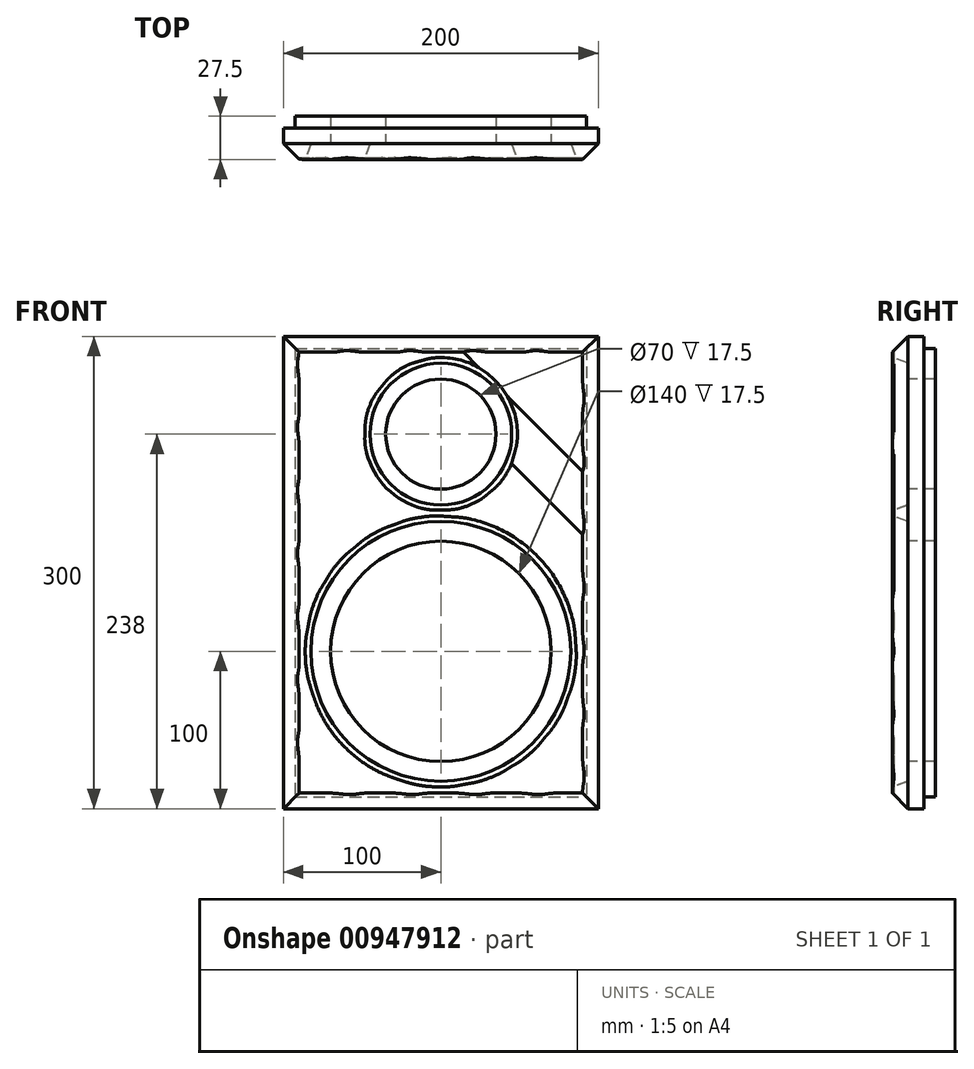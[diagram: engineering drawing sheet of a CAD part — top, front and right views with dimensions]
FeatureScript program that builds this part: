
annotation { "Feature Type Name" : "Feature", "Feature Type Description" : "" }
export const myFeature = defineFeature(function(context is Context, id is Id, definition is map)
    precondition{}
    {
        {
            var Q0;
            Q0=qCreatedBy(makeId("Right.planeOp"),FACE);
            cPlane(context, id + "F0", {"entities" : qUnion([Q0]), "cplaneType" : CPlaneType.OFFSET, "offset" : 100 * mm, "width" : 150 * mm, "height" : 150 * mm});
        }
        {
            var Q0;
            Q0=qCreatedBy(makeId("Right.planeOp"),FACE);
            cPlane(context, id + "F1", {"entities" : qUnion([Q0]), "cplaneType" : CPlaneType.OFFSET, "offset" : 100 * mm, "oppositeDirection" : true, "width" : 150 * mm, "height" : 150 * mm});
        }
        {
            var Q0;
            Q0=qCreatedBy(makeId("Right.planeOp"),FACE);
            cPlane(context, id + "F2", {"entities" : qUnion([Q0]), "cplaneType" : CPlaneType.OFFSET, "offset" : (100 - 7.5) * mm, "width" : 150 * mm, "height" : 150 * mm});
        }
        {
            var Q0;
            Q0=qCreatedBy(makeId("Right.planeOp"),FACE);
            cPlane(context, id + "F3", {"entities" : qUnion([Q0]), "cplaneType" : CPlaneType.OFFSET, "offset" : (100 - 7.5) * mm, "oppositeDirection" : true, "width" : 150 * mm, "height" : 150 * mm});
        }
        {
            var Q0;
            Q0=qCreatedBy(makeId("Top.planeOp"),FACE);
            cPlane(context, id + "F4", {"entities" : qUnion([Q0]), "cplaneType" : CPlaneType.OFFSET, "offset" : 7.7 * mm, "width" : 150 * mm, "height" : 150 * mm});
        }
        {
            var Q0;
            Q0=qCreatedBy(makeId("Top.planeOp"),FACE);
            cPlane(context, id + "F5", {"entities" : qUnion([Q0]), "cplaneType" : CPlaneType.OFFSET, "offset" : 300 * mm, "width" : 150 * mm, "height" : 150 * mm});
        }
        {
            var Q0;
            Q0=qCreatedBy(makeId("Top.planeOp"),FACE);
            cPlane(context, id + "F6", {"entities" : qUnion([Q0]), "cplaneType" : CPlaneType.OFFSET, "offset" : (300 - 7.5) * mm, "width" : 150 * mm, "height" : 150 * mm});
        }
        {
            var Q0;
            Q0=qCreatedBy(makeId("Front.planeOp"),FACE);
            cPlane(context, id + "F7", {"entities" : qUnion([Q0]), "cplaneType" : CPlaneType.OFFSET, "offset" : 150 * mm, "width" : 150 * mm, "height" : 150 * mm});
        }
        {
            var Q0;
            Q0=qCreatedBy(makeId("Front.planeOp"),FACE);
            cPlane(context, id + "F8", {"entities" : qUnion([Q0]), "cplaneType" : CPlaneType.OFFSET, "offset" : (150 - 7.5) * mm, "width" : 150 * mm, "height" : 150 * mm});
        }
        {
            var Q0;
            Q0=qCreatedBy(id+"F8.planeOp",FACE);
            var sketch = newSketch(context, id + "F9", { "sketchPlane" : qUnion([Q0])});
            skLineSegment(sketch, "E0.bottom", {"start": v(-92.5, 292.5) * mm, "end": v(92.5, 292.5) * mm});
            skLineSegment(sketch, "E0.top", {"start": v(-92.5, 7.7) * mm, "end": v(92.5, 7.7) * mm});
            skLineSegment(sketch, "E0.left", {"start": v(-92.5, 292.5) * mm, "end": v(-92.5, 7.7) * mm});
            skLineSegment(sketch, "E0.right", {"start": v(92.5, 292.5) * mm, "end": v(92.5, 7.7) * mm});
            skSolve(sketch);
        }
        {
            var Q0;
            Q0=makeQuery(id+"F9.imprint","IMPRINT",FACE,{"disambiguationData":[TD([[makeQuery(id+"F9.imprint","IMPRINT",EDGE,{"derivedFrom":sQuery(id+"F9.wireOp",EDGE,"E0.bottom")}),-1.0]])]});
            extrude(context, id + "F10", {"entities" : qUnion([Q0]), "depth" : 7.5 * mm, "offsetDistance" : 25 * mm});
        }
        {
            var Q0;
            Q0=qCreatedBy(id+"F7.planeOp",FACE);
            var sketch = newSketch(context, id + "F11", { "sketchPlane" : qUnion([Q0])});
            skLineSegment(sketch, "E1.bottom", {"start": v(-100, 300) * mm, "end": v(100, 300) * mm});
            skLineSegment(sketch, "E1.top", {"start": v(-100, 0) * mm, "end": v(100, 0) * mm});
            skLineSegment(sketch, "E1.left", {"start": v(-100, 300) * mm, "end": v(-100, 0) * mm});
            skLineSegment(sketch, "E1.right", {"start": v(100, 300) * mm, "end": v(100, 0) * mm});
            skSolve(sketch);
        }
        {
            var Q0;
            Q0=makeQuery(id+"F11.imprint","IMPRINT",FACE,{"disambiguationData":[TD([[makeQuery(id+"F11.imprint","IMPRINT",EDGE,{"derivedFrom":sQuery(id+"F11.wireOp",EDGE,"E1.bottom")}),-1.0]])]});
            extrude(context, id + "F12", {"entities" : qUnion([Q0]), "operationType" : NewBodyOperationType.ADD, "depth" : 20 * mm, "offsetDistance" : 25 * mm});
        }
        {
            var Q0;
            Q0=qCreatedBy(id+"F0.planeOp",FACE);
            var sketch = newSketch(context, id + "F13", { "sketchPlane" : qUnion([Q0])});
            skLineSegment(sketch, "E2", {"start": v(-220, 0) * mm, "end": v(-220, 300) * mm});
            skLineSegment(sketch, "E3", {"start": v(-220, 300) * mm, "end": v(-180, 300) * mm});
            skLineSegment(sketch, "E4", {"start": v(-180, 300) * mm, "end": v(-180, 0) * mm});
            skLineSegment(sketch, "E5", {"start": v(-180, 0) * mm, "end": v(-220, 0) * mm});
            skSolve(sketch);
        }
        {
            var Q0;
            Q0=qCreatedBy(makeId("Front.planeOp"),FACE);
            cPlane(context, id + "F14", {"entities" : qUnion([Q0]), "cplaneType" : CPlaneType.OFFSET, "offset" : 300 * mm, "width" : 150 * mm, "height" : 150 * mm});
        }
        {
            var Q0;
            Q0=qCreatedBy(makeId("Front.planeOp"),FACE);
            cPlane(context, id + "F15", {"entities" : qUnion([Q0]), "cplaneType" : CPlaneType.OFFSET, "offset" : 160 * mm, "width" : 150 * mm, "height" : 150 * mm});
        }
        {
            var Q0;
            Q0=qCreatedBy(id+"F14.planeOp",FACE);
            var sketch = newSketch(context, id + "F16", { "sketchPlane" : qUnion([Q0])});
            skCircle(sketch, "E6", {"center": v(0, 100) * mm, "radius": 70 * mm});
            skSolve(sketch);
        }
        {
            var Q0;
            Q0=qSketchRegion(id+"F16",true);
            var Q1;
            Q1=qCreatedBy(id+"F8.planeOp",FACE);
            extrude(context, id + "F17", {"entities" : qUnion([Q0]), "operationType" : NewBodyOperationType.REMOVE, "endBound" : BoundingType.UP_TO_SURFACE, "oppositeDirection" : true, "depth" : 25 * mm, "endBoundEntityFace" : qUnion([Q1]), "offsetDistance" : 25 * mm});
        }
        {
            var Q0;
            Q0=qCreatedBy(id+"F14.planeOp",FACE);
            var sketch = newSketch(context, id + "F18", { "sketchPlane" : qUnion([Q0])});
            skCircle(sketch, "E7", {"center": v(0, 100) * mm, "radius": 82.5 * mm});
            skSolve(sketch);
        }
        {
            var Q0;
            Q0=qSketchRegion(id+"F18",true);
            var Q1;
            Q1=qCreatedBy(id+"F15.planeOp",FACE);
            extrude(context, id + "F19", {"entities" : qUnion([Q0]), "operationType" : NewBodyOperationType.REMOVE, "endBound" : BoundingType.UP_TO_SURFACE, "oppositeDirection" : true, "depth" : 25 * mm, "endBoundEntityFace" : qUnion([Q1]), "offsetDistance" : 25 * mm});
        }
        {
            var Q0;
            Q0=qCreatedBy(id+"F14.planeOp",FACE);
            var sketch = newSketch(context, id + "F20", { "sketchPlane" : qUnion([Q0])});
            skCircle(sketch, "E8", {"center": v(0, 238) * mm, "radius": 35 * mm});
            skSolve(sketch);
        }
        {
            var Q0;
            Q0=makeQuery(id+"F20.imprint","IMPRINT",FACE,{"disambiguationData":[TD([[makeQuery(id+"F20.imprint","IMPRINT",EDGE,{"derivedFrom":sQuery(id+"F20.wireOp",EDGE,"E8")}),1.0]])]});
            var Q1;
            Q1=qCreatedBy(id+"F8.planeOp",FACE);
            extrude(context, id + "F21", {"entities" : qUnion([Q0]), "operationType" : NewBodyOperationType.REMOVE, "endBound" : BoundingType.UP_TO_SURFACE, "oppositeDirection" : true, "depth" : 25 * mm, "endBoundEntityFace" : qUnion([Q1]), "offsetDistance" : 25 * mm});
        }
        {
            var Q0;
            Q0=qCreatedBy(id+"F14.planeOp",FACE);
            var sketch = newSketch(context, id + "F22", { "sketchPlane" : qUnion([Q0])});
            skCircle(sketch, "E9", {"center": v(0, 238) * mm, "radius": 45 * mm});
            skSolve(sketch);
        }
        {
            var Q0;
            Q0=qSketchRegion(id+"F22",true);
            var Q1;
            Q1=qCreatedBy(id+"F15.planeOp",FACE);
            extrude(context, id + "F23", {"entities" : qUnion([Q0]), "operationType" : NewBodyOperationType.REMOVE, "endBound" : BoundingType.UP_TO_SURFACE, "oppositeDirection" : true, "depth" : 25 * mm, "endBoundEntityFace" : qUnion([Q1]), "offsetDistance" : 25 * mm});
        }
        {
            var Q0;
            Q0=makeQuery(id+"F13.imprint","IMPRINT",FACE,{"disambiguationData":[TD([[makeQuery(id+"F13.imprint","IMPRINT",EDGE,{"derivedFrom":sQuery(id+"F13.wireOp",EDGE,"E2")}),-1.0]])]});
            var Q1;
            Q1=qCreatedBy(id+"F1.planeOp",FACE);
            extrude(context, id + "F24", {"entities" : qUnion([Q0]), "operationType" : NewBodyOperationType.REMOVE, "endBound" : BoundingType.UP_TO_SURFACE, "oppositeDirection" : true, "depth" : 25 * mm, "endBoundEntityFace" : qUnion([Q1]), "offsetDistance" : 25 * mm});
        }
        {
            var Q0;
            Q0=makeQuery(id+"F12.opExtrude","CAP_EDGE",EDGE,{"disambiguationData":[OSD([sQuery(id+"F11.wireOp",EDGE,"E1.right")])],"isStart":false});
            var Q1;
            Q1=makeQuery(id+"F12.opExtrude","CAP_EDGE",EDGE,{"disambiguationData":[OSD([sQuery(id+"F11.wireOp",EDGE,"E1.bottom")])],"isStart":false});
            var Q2;
            Q2=makeQuery(id+"F12.opExtrude","CAP_EDGE",EDGE,{"disambiguationData":[OSD([sQuery(id+"F11.wireOp",EDGE,"E1.left")])],"isStart":false});
            var Q3;
            Q3=makeQuery(id+"F12.opExtrude","CAP_EDGE",EDGE,{"disambiguationData":[OSD([sQuery(id+"F11.wireOp",EDGE,"E1.top")])],"isStart":false});
            chamfer(context, id + "F25", {"entities" : qUnion([Q0, Q1, Q2, Q3]), "width" : 10 * mm, "tangentPropagation" : true});
        }
        {
            var Q0;
            Q0=makeQuery(id+"F19.boolean.opBoolean","INTERSECT",EDGE,{"derivedFrom":[makeQuery(id+"F12.opExtrude","CAP_FACE",FACE,{"disambiguationData":[OSD([sQuery(id+"F11.wireOp",EDGE,"E1.bottom"),sQuery(id+"F11.wireOp",EDGE,"E1.top"),sQuery(id+"F11.wireOp",EDGE,"E1.left"),sQuery(id+"F11.wireOp",EDGE,"E1.right")])],"isStart":false}),makeQuery(id+"F19.opExtrude","SWEPT_FACE",FACE,{"disambiguationData":[OSD([sQuery(id+"F18.wireOp",EDGE,"E7")])]})]});
            chamfer(context, id + "F26", {"entities" : qUnion([Q0]), "chamferType" : ChamferType.OFFSET_ANGLE, "width" : 10 * mm, "oppositeDirection" : false, "angle" : 20 * degree, "tangentPropagation" : true});
        }
        {
            var Q0;
            Q0=makeQuery(id+"F23.boolean.opBoolean","INTERSECT",EDGE,{"derivedFrom":[makeQuery(id+"F12.opExtrude","CAP_FACE",FACE,{"disambiguationData":[OSD([sQuery(id+"F11.wireOp",EDGE,"E1.bottom"),sQuery(id+"F11.wireOp",EDGE,"E1.top"),sQuery(id+"F11.wireOp",EDGE,"E1.left"),sQuery(id+"F11.wireOp",EDGE,"E1.right")])],"isStart":false}),makeQuery(id+"F23.opExtrude","SWEPT_FACE",FACE,{"disambiguationData":[OSD([sQuery(id+"F22.wireOp",EDGE,"E9")])]})]});
            chamfer(context, id + "F27", {"entities" : qUnion([Q0]), "chamferType" : ChamferType.OFFSET_ANGLE, "width" : 10 * mm, "oppositeDirection" : false, "angle" : 20 * degree, "tangentPropagation" : true});
        }
        {
            var Q0;
            Q0=qCreatedBy(id+"F14.planeOp",FACE);
            var sketch = newSketch(context, id + "F28", { "sketchPlane" : qUnion([Q0])});
            skLineSegment(sketch, "E10.bottom", {"start": v(-205.06, 643.47) * mm, "end": v(268.7, 169.7) * mm});
            skLineSegment(sketch, "E10.top", {"start": v(-212.13, 636.4) * mm, "end": v(261.63, 162.63) * mm});
            skLineSegment(sketch, "E10.left", {"start": v(-205.06, 643.47) * mm, "end": v(-212.13, 636.4) * mm});
            skLineSegment(sketch, "E10.right", {"start": v(268.7, 169.7) * mm, "end": v(261.63, 162.63) * mm});
            skLineSegment(sketch, "E11.0.1.0", {"start": v(-205.06, 603.47) * mm, "end": v(268.7, 129.7) * mm});
            skLineSegment(sketch, "E11.0.1.1", {"start": v(-212.13, 596.4) * mm, "end": v(261.63, 122.63) * mm});
            skLineSegment(sketch, "E11.0.1.2", {"start": v(-205.06, 603.47) * mm, "end": v(-212.13, 596.4) * mm});
            skLineSegment(sketch, "E11.0.1.3", {"start": v(268.7, 129.7) * mm, "end": v(261.63, 122.63) * mm});
            skLineSegment(sketch, "E11.0.2.0", {"start": v(-205.06, 563.47) * mm, "end": v(268.7, 89.7) * mm});
            skLineSegment(sketch, "E11.0.2.1", {"start": v(-212.13, 556.4) * mm, "end": v(261.63, 82.63) * mm});
            skLineSegment(sketch, "E11.0.2.2", {"start": v(-205.06, 563.47) * mm, "end": v(-212.13, 556.4) * mm});
            skLineSegment(sketch, "E11.0.2.3", {"start": v(268.7, 89.7) * mm, "end": v(261.63, 82.63) * mm});
            skLineSegment(sketch, "E11.0.3.0", {"start": v(-205.06, 523.47) * mm, "end": v(268.7, 49.7) * mm});
            skLineSegment(sketch, "E11.0.3.1", {"start": v(-212.13, 516.4) * mm, "end": v(261.63, 42.63) * mm});
            skLineSegment(sketch, "E11.0.3.2", {"start": v(-205.06, 523.47) * mm, "end": v(-212.13, 516.4) * mm});
            skLineSegment(sketch, "E11.0.3.3", {"start": v(268.7, 49.7) * mm, "end": v(261.63, 42.63) * mm});
            skLineSegment(sketch, "E11.0.4.0", {"start": v(-205.06, 483.47) * mm, "end": v(268.7, 9.7) * mm});
            skLineSegment(sketch, "E11.0.4.1", {"start": v(-212.13, 476.4) * mm, "end": v(261.63, 2.63) * mm});
            skLineSegment(sketch, "E11.0.4.2", {"start": v(-205.06, 483.47) * mm, "end": v(-212.13, 476.4) * mm});
            skLineSegment(sketch, "E11.0.4.3", {"start": v(268.7, 9.7) * mm, "end": v(261.63, 2.63) * mm});
            skLineSegment(sketch, "E11.0.5.0", {"start": v(-205.06, 443.47) * mm, "end": v(268.7, -30.3) * mm});
            skLineSegment(sketch, "E11.0.5.1", {"start": v(-212.13, 436.4) * mm, "end": v(261.63, -37.37) * mm});
            skLineSegment(sketch, "E11.0.5.2", {"start": v(-205.06, 443.47) * mm, "end": v(-212.13, 436.4) * mm});
            skLineSegment(sketch, "E11.0.5.3", {"start": v(268.7, -30.3) * mm, "end": v(261.63, -37.37) * mm});
            skLineSegment(sketch, "E11.0.6.0", {"start": v(-205.06, 403.47) * mm, "end": v(268.7, -70.3) * mm});
            skLineSegment(sketch, "E11.0.6.1", {"start": v(-212.13, 396.4) * mm, "end": v(261.63, -77.37) * mm});
            skLineSegment(sketch, "E11.0.6.2", {"start": v(-205.06, 403.47) * mm, "end": v(-212.13, 396.4) * mm});
            skLineSegment(sketch, "E11.0.6.3", {"start": v(268.7, -70.3) * mm, "end": v(261.63, -77.37) * mm});
            skLineSegment(sketch, "E11.0.7.0", {"start": v(-205.06, 363.47) * mm, "end": v(268.7, -110.3) * mm});
            skLineSegment(sketch, "E11.0.7.1", {"start": v(-212.13, 356.4) * mm, "end": v(261.63, -117.37) * mm});
            skLineSegment(sketch, "E11.0.7.2", {"start": v(-205.06, 363.47) * mm, "end": v(-212.13, 356.4) * mm});
            skLineSegment(sketch, "E11.0.7.3", {"start": v(268.7, -110.3) * mm, "end": v(261.63, -117.37) * mm});
            skLineSegment(sketch, "E11.0.8.0", {"start": v(-205.06, 323.47) * mm, "end": v(268.7, -150.3) * mm});
            skLineSegment(sketch, "E11.0.8.1", {"start": v(-212.13, 316.4) * mm, "end": v(261.63, -157.37) * mm});
            skLineSegment(sketch, "E11.0.8.2", {"start": v(-205.06, 323.47) * mm, "end": v(-212.13, 316.4) * mm});
            skLineSegment(sketch, "E11.0.8.3", {"start": v(268.7, -150.3) * mm, "end": v(261.63, -157.37) * mm});
            skLineSegment(sketch, "E11.0.9.0", {"start": v(-205.06, 283.47) * mm, "end": v(268.7, -190.3) * mm});
            skLineSegment(sketch, "E11.0.9.1", {"start": v(-212.13, 276.4) * mm, "end": v(261.63, -197.37) * mm});
            skLineSegment(sketch, "E11.0.9.2", {"start": v(-205.06, 283.47) * mm, "end": v(-212.13, 276.4) * mm});
            skLineSegment(sketch, "E11.0.9.3", {"start": v(268.7, -190.3) * mm, "end": v(261.63, -197.37) * mm});
            skLineSegment(sketch, "E11.0.10.0", {"start": v(-205.06, 243.47) * mm, "end": v(268.7, -230.3) * mm});
            skLineSegment(sketch, "E11.0.10.1", {"start": v(-212.13, 236.4) * mm, "end": v(261.63, -237.37) * mm});
            skLineSegment(sketch, "E11.0.10.2", {"start": v(-205.06, 243.47) * mm, "end": v(-212.13, 236.4) * mm});
            skLineSegment(sketch, "E11.0.10.3", {"start": v(268.7, -230.3) * mm, "end": v(261.63, -237.37) * mm});
            skLineSegment(sketch, "E11.0.11.0", {"start": v(-205.06, 203.47) * mm, "end": v(268.7, -270.3) * mm});
            skLineSegment(sketch, "E11.0.11.1", {"start": v(-212.13, 196.4) * mm, "end": v(261.63, -277.37) * mm});
            skLineSegment(sketch, "E11.0.11.2", {"start": v(-205.06, 203.47) * mm, "end": v(-212.13, 196.4) * mm});
            skLineSegment(sketch, "E11.0.11.3", {"start": v(268.7, -270.3) * mm, "end": v(261.63, -277.37) * mm});
            skLineSegment(sketch, "E11.0.12.0", {"start": v(-205.06, 163.47) * mm, "end": v(268.7, -310.3) * mm});
            skLineSegment(sketch, "E11.0.12.1", {"start": v(-212.13, 156.4) * mm, "end": v(261.63, -317.37) * mm});
            skLineSegment(sketch, "E11.0.12.2", {"start": v(-205.06, 163.47) * mm, "end": v(-212.13, 156.4) * mm});
            skLineSegment(sketch, "E11.0.12.3", {"start": v(268.7, -310.3) * mm, "end": v(261.63, -317.37) * mm});
            skLineSegment(sketch, "E11.0.13.0", {"start": v(-205.06, 123.47) * mm, "end": v(268.7, -350.3) * mm});
            skLineSegment(sketch, "E11.0.13.1", {"start": v(-212.13, 116.4) * mm, "end": v(261.63, -357.37) * mm});
            skLineSegment(sketch, "E11.0.13.2", {"start": v(-205.06, 123.47) * mm, "end": v(-212.13, 116.4) * mm});
            skLineSegment(sketch, "E11.0.13.3", {"start": v(268.7, -350.3) * mm, "end": v(261.63, -357.37) * mm});
            skLineSegment(sketch, "E11.0.14.0", {"start": v(-205.06, 83.47) * mm, "end": v(268.7, -390.3) * mm});
            skLineSegment(sketch, "E11.0.14.1", {"start": v(-212.13, 76.4) * mm, "end": v(261.63, -397.37) * mm});
            skLineSegment(sketch, "E11.0.14.2", {"start": v(-205.06, 83.47) * mm, "end": v(-212.13, 76.4) * mm});
            skLineSegment(sketch, "E11.0.14.3", {"start": v(268.7, -390.3) * mm, "end": v(261.63, -397.37) * mm});
            skLineSegment(sketch, "E11.direction1", {"start": v(261.63, 162.63) * mm, "end": v(286.63, 162.63) * mm, "construction": true});
            skLineSegment(sketch, "E11.direction2", {"start": v(261.63, 162.63) * mm, "end": v(261.63, 122.63) * mm, "construction": true});
            skSolve(sketch);
        }
        {
            var Q0;
            Q0=makeQuery(id+"F28.imprint","IMPRINT",FACE,{"disambiguationData":[TD([[makeQuery(id+"F28.imprint","IMPRINT",EDGE,{"derivedFrom":sQuery(id+"F28.wireOp",EDGE,"E11.0.8.0")}),-1.0]])]});
            var Q1;
            Q1=makeQuery(id+"F28.imprint","IMPRINT",FACE,{"disambiguationData":[TD([[makeQuery(id+"F28.imprint","IMPRINT",EDGE,{"derivedFrom":sQuery(id+"F28.wireOp",EDGE,"E10.bottom")}),-1.0]])]});
            var Q2;
            Q2=makeQuery(id+"F28.imprint","IMPRINT",FACE,{"disambiguationData":[TD([[makeQuery(id+"F28.imprint","IMPRINT",EDGE,{"derivedFrom":sQuery(id+"F28.wireOp",EDGE,"E11.0.1.0")}),-1.0]])]});
            var Q3;
            Q3=makeQuery(id+"F28.imprint","IMPRINT",FACE,{"disambiguationData":[TD([[makeQuery(id+"F28.imprint","IMPRINT",EDGE,{"derivedFrom":sQuery(id+"F28.wireOp",EDGE,"E11.0.2.0")}),-1.0]])]});
            var Q4;
            Q4=makeQuery(id+"F28.imprint","IMPRINT",FACE,{"disambiguationData":[TD([[makeQuery(id+"F28.imprint","IMPRINT",EDGE,{"derivedFrom":sQuery(id+"F28.wireOp",EDGE,"E11.0.3.0")}),-1.0]])]});
            var Q5;
            Q5=makeQuery(id+"F28.imprint","IMPRINT",FACE,{"disambiguationData":[TD([[makeQuery(id+"F28.imprint","IMPRINT",EDGE,{"derivedFrom":sQuery(id+"F28.wireOp",EDGE,"E11.0.4.0")}),-1.0]])]});
            var Q6;
            Q6=makeQuery(id+"F28.imprint","IMPRINT",FACE,{"disambiguationData":[TD([[makeQuery(id+"F28.imprint","IMPRINT",EDGE,{"derivedFrom":sQuery(id+"F28.wireOp",EDGE,"E11.0.5.0")}),-1.0]])]});
            var Q7;
            Q7=makeQuery(id+"F28.imprint","IMPRINT",FACE,{"disambiguationData":[TD([[makeQuery(id+"F28.imprint","IMPRINT",EDGE,{"derivedFrom":sQuery(id+"F28.wireOp",EDGE,"E11.0.6.0")}),-1.0]])]});
            var Q8;
            Q8=makeQuery(id+"F28.imprint","IMPRINT",FACE,{"disambiguationData":[TD([[makeQuery(id+"F28.imprint","IMPRINT",EDGE,{"derivedFrom":sQuery(id+"F28.wireOp",EDGE,"E11.0.7.0")}),-1.0]])]});
            var Q9;
            Q9=makeQuery(id+"F28.imprint","IMPRINT",FACE,{"disambiguationData":[TD([[makeQuery(id+"F28.imprint","IMPRINT",EDGE,{"derivedFrom":sQuery(id+"F28.wireOp",EDGE,"E11.0.9.0")}),-1.0]])]});
            var Q10;
            Q10=makeQuery(id+"F28.imprint","IMPRINT",FACE,{"disambiguationData":[TD([[makeQuery(id+"F28.imprint","IMPRINT",EDGE,{"derivedFrom":sQuery(id+"F28.wireOp",EDGE,"E11.0.10.0")}),-1.0]])]});
            var Q11;
            Q11=makeQuery(id+"F28.imprint","IMPRINT",FACE,{"disambiguationData":[TD([[makeQuery(id+"F28.imprint","IMPRINT",EDGE,{"derivedFrom":sQuery(id+"F28.wireOp",EDGE,"E11.0.11.0")}),-1.0]])]});
            var Q12;
            Q12=makeQuery(id+"F28.imprint","IMPRINT",FACE,{"disambiguationData":[TD([[makeQuery(id+"F28.imprint","IMPRINT",EDGE,{"derivedFrom":sQuery(id+"F28.wireOp",EDGE,"E11.0.12.0")}),-1.0]])]});
            var Q13;
            Q13=makeQuery(id+"F28.imprint","IMPRINT",FACE,{"disambiguationData":[TD([[makeQuery(id+"F28.imprint","IMPRINT",EDGE,{"derivedFrom":sQuery(id+"F28.wireOp",EDGE,"E11.0.13.0")}),-1.0]])]});
            extrude(context, id + "F29", {"entities" : qUnion([Q0, Q1, Q2, Q3, Q4, Q5, Q6, Q7, Q8, Q9, Q10, Q11, Q12, Q13]), "operationType" : NewBodyOperationType.REMOVE, "oppositeDirection" : true, "depth" : 131 * mm, "offsetDistance" : 25 * mm});
        }
        {
            var Q0;
            Q0=makeQuery(id+"F29.boolean.opBoolean","COPY",EDGE,{"derivedFrom":makeQuery(id+"F29.opExtrude","CAP_EDGE",EDGE,{"disambiguationData":[OSD([sQuery(id+"F28.wireOp",EDGE,"E11.0.3.0")])],"isStart":false})});
            var Q1;
            {var subQ0=sQuery(id+"F11.wireOp",EDGE,"E1.right");var subQ1=sQuery(id+"F28.wireOp",EDGE,"E11.0.4.0");Q1=makeQuery(id+"F29.boolean.opBoolean","COPY",EDGE,{"disambiguationData":[TD([makeQuery(id+"F25.opChamfer","BLEND_FACE",FACE,{"disambiguationData":[OSD([subQ0])]})])],"derivedFrom":makeQuery(id+"F29.opExtrude","CAP_EDGE",EDGE,{"disambiguationData":[OSD([subQ1])],"isStart":false})});}
            var Q2;
            {var subQ0=sQuery(id+"F11.wireOp",EDGE,"E1.right");var subQ1=sQuery(id+"F28.wireOp",EDGE,"E11.0.5.0");Q2=makeQuery(id+"F29.boolean.opBoolean","COPY",EDGE,{"disambiguationData":[TD([makeQuery(id+"F25.opChamfer","BLEND_FACE",FACE,{"disambiguationData":[OSD([subQ0])]})])],"derivedFrom":makeQuery(id+"F29.opExtrude","CAP_EDGE",EDGE,{"disambiguationData":[OSD([subQ1])],"isStart":false})});}
            var Q3;
            {var subQ0=sQuery(id+"F11.wireOp",EDGE,"E1.right");var subQ1=sQuery(id+"F28.wireOp",EDGE,"E11.0.6.0");Q3=makeQuery(id+"F29.boolean.opBoolean","COPY",EDGE,{"disambiguationData":[TD([makeQuery(id+"F25.opChamfer","BLEND_FACE",FACE,{"disambiguationData":[OSD([subQ0])]}),makeQuery(id+"F26.opChamfer","BLEND_FACE",FACE,{"disambiguationData":[OSD([sQuery(id+"F11.wireOp",EDGE,"E1.bottom"),sQuery(id+"F11.wireOp",EDGE,"E1.top"),sQuery(id+"F11.wireOp",EDGE,"E1.left"),subQ0,sQuery(id+"F18.wireOp",EDGE,"E7")])]}),makeQuery(id+"F29.opExtrude","SWEPT_FACE",FACE,{"disambiguationData":[OSD([subQ1])]}),makeQuery(id+"F29.opExtrude","CAP_FACE",FACE,{"disambiguationData":[OSD([subQ1,sQuery(id+"F28.wireOp",EDGE,"E11.0.6.1"),sQuery(id+"F28.wireOp",EDGE,"E11.0.6.2"),sQuery(id+"F28.wireOp",EDGE,"E11.0.6.3")])],"isStart":false})])],"derivedFrom":makeQuery(id+"F29.opExtrude","CAP_EDGE",EDGE,{"disambiguationData":[OSD([subQ1])],"isStart":false})});}
            var Q4;
            {var subQ0=sQuery(id+"F11.wireOp",EDGE,"E1.right");var subQ1=sQuery(id+"F11.wireOp",EDGE,"E1.left");var subQ2=sQuery(id+"F11.wireOp",EDGE,"E1.top");var subQ3=sQuery(id+"F11.wireOp",EDGE,"E1.bottom");var subQ4=sQuery(id+"F28.wireOp",EDGE,"E11.0.6.0");Q4=makeQuery(id+"F29.boolean.opBoolean","COPY",EDGE,{"disambiguationData":[TD([makeQuery(id+"F26.opChamfer","BLEND_FACE",FACE,{"disambiguationData":[OSD([subQ3,subQ2,subQ1,subQ0,sQuery(id+"F18.wireOp",EDGE,"E7")])]}),makeQuery(id+"F27.opChamfer","BLEND_FACE",FACE,{"disambiguationData":[OSD([subQ3,subQ2,subQ1,subQ0,sQuery(id+"F22.wireOp",EDGE,"E9")])]}),makeQuery(id+"F29.opExtrude","SWEPT_FACE",FACE,{"disambiguationData":[OSD([subQ4])]}),makeQuery(id+"F29.opExtrude","CAP_FACE",FACE,{"disambiguationData":[OSD([subQ4,sQuery(id+"F28.wireOp",EDGE,"E11.0.6.1"),sQuery(id+"F28.wireOp",EDGE,"E11.0.6.2"),sQuery(id+"F28.wireOp",EDGE,"E11.0.6.3")])],"isStart":false})])],"derivedFrom":makeQuery(id+"F29.opExtrude","CAP_EDGE",EDGE,{"disambiguationData":[OSD([subQ4])],"isStart":false})});}
            var Q5;
            {var subQ0=sQuery(id+"F11.wireOp",EDGE,"E1.bottom");var subQ1=sQuery(id+"F28.wireOp",EDGE,"E11.0.4.0");Q5=makeQuery(id+"F29.boolean.opBoolean","COPY",EDGE,{"disambiguationData":[TD([makeQuery(id+"F25.opChamfer","BLEND_FACE",FACE,{"disambiguationData":[OSD([subQ0])]})])],"derivedFrom":makeQuery(id+"F29.opExtrude","CAP_EDGE",EDGE,{"disambiguationData":[OSD([subQ1])],"isStart":false})});}
            var Q6;
            {var subQ0=sQuery(id+"F11.wireOp",EDGE,"E1.bottom");var subQ1=sQuery(id+"F28.wireOp",EDGE,"E11.0.5.0");Q6=makeQuery(id+"F29.boolean.opBoolean","COPY",EDGE,{"disambiguationData":[TD([makeQuery(id+"F25.opChamfer","BLEND_FACE",FACE,{"disambiguationData":[OSD([subQ0])]})])],"derivedFrom":makeQuery(id+"F29.opExtrude","CAP_EDGE",EDGE,{"disambiguationData":[OSD([subQ1])],"isStart":false})});}
            var Q7;
            {var subQ0=sQuery(id+"F11.wireOp",EDGE,"E1.left");var subQ1=sQuery(id+"F28.wireOp",EDGE,"E11.0.6.0");Q7=makeQuery(id+"F29.boolean.opBoolean","COPY",EDGE,{"disambiguationData":[TD([makeQuery(id+"F25.opChamfer","BLEND_FACE",FACE,{"disambiguationData":[OSD([subQ0])]}),makeQuery(id+"F27.opChamfer","BLEND_FACE",FACE,{"disambiguationData":[OSD([sQuery(id+"F11.wireOp",EDGE,"E1.bottom"),sQuery(id+"F11.wireOp",EDGE,"E1.top"),subQ0,sQuery(id+"F11.wireOp",EDGE,"E1.right"),sQuery(id+"F22.wireOp",EDGE,"E9")])]}),makeQuery(id+"F29.opExtrude","SWEPT_FACE",FACE,{"disambiguationData":[OSD([subQ1])]}),makeQuery(id+"F29.opExtrude","CAP_FACE",FACE,{"disambiguationData":[OSD([subQ1,sQuery(id+"F28.wireOp",EDGE,"E11.0.6.1"),sQuery(id+"F28.wireOp",EDGE,"E11.0.6.2"),sQuery(id+"F28.wireOp",EDGE,"E11.0.6.3")])],"isStart":false})])],"derivedFrom":makeQuery(id+"F29.opExtrude","CAP_EDGE",EDGE,{"disambiguationData":[OSD([subQ1])],"isStart":false})});}
            var Q8;
            {var subQ0=sQuery(id+"F11.wireOp",EDGE,"E1.left");var subQ1=sQuery(id+"F28.wireOp",EDGE,"E11.0.7.0");Q8=makeQuery(id+"F29.boolean.opBoolean","COPY",EDGE,{"disambiguationData":[TD([makeQuery(id+"F25.opChamfer","BLEND_FACE",FACE,{"disambiguationData":[OSD([subQ0])]})])],"derivedFrom":makeQuery(id+"F29.opExtrude","CAP_EDGE",EDGE,{"disambiguationData":[OSD([subQ1])],"isStart":false})});}
            var Q9;
            {var subQ0=sQuery(id+"F11.wireOp",EDGE,"E1.left");var subQ1=sQuery(id+"F28.wireOp",EDGE,"E11.0.8.0");Q9=makeQuery(id+"F29.boolean.opBoolean","COPY",EDGE,{"disambiguationData":[TD([makeQuery(id+"F25.opChamfer","BLEND_FACE",FACE,{"disambiguationData":[OSD([subQ0])]})])],"derivedFrom":makeQuery(id+"F29.opExtrude","CAP_EDGE",EDGE,{"disambiguationData":[OSD([subQ1])],"isStart":false})});}
            var Q10;
            {var subQ0=sQuery(id+"F11.wireOp",EDGE,"E1.left");var subQ1=sQuery(id+"F28.wireOp",EDGE,"E11.0.9.0");Q10=makeQuery(id+"F29.boolean.opBoolean","COPY",EDGE,{"disambiguationData":[TD([makeQuery(id+"F25.opChamfer","BLEND_FACE",FACE,{"disambiguationData":[OSD([subQ0])]})])],"derivedFrom":makeQuery(id+"F29.opExtrude","CAP_EDGE",EDGE,{"disambiguationData":[OSD([subQ1])],"isStart":false})});}
            var Q11;
            {var subQ0=sQuery(id+"F11.wireOp",EDGE,"E1.left");var subQ1=sQuery(id+"F28.wireOp",EDGE,"E11.0.10.0");Q11=makeQuery(id+"F29.boolean.opBoolean","COPY",EDGE,{"disambiguationData":[TD([makeQuery(id+"F25.opChamfer","BLEND_FACE",FACE,{"disambiguationData":[OSD([subQ0])]})])],"derivedFrom":makeQuery(id+"F29.opExtrude","CAP_EDGE",EDGE,{"disambiguationData":[OSD([subQ1])],"isStart":false})});}
            var Q12;
            {var subQ0=sQuery(id+"F11.wireOp",EDGE,"E1.left");var subQ1=sQuery(id+"F28.wireOp",EDGE,"E11.0.11.0");Q12=makeQuery(id+"F29.boolean.opBoolean","COPY",EDGE,{"disambiguationData":[TD([makeQuery(id+"F25.opChamfer","BLEND_FACE",FACE,{"disambiguationData":[OSD([subQ0])]})])],"derivedFrom":makeQuery(id+"F29.opExtrude","CAP_EDGE",EDGE,{"disambiguationData":[OSD([subQ1])],"isStart":false})});}
            var Q13;
            Q13=makeQuery(id+"F29.boolean.opBoolean","COPY",EDGE,{"derivedFrom":makeQuery(id+"F29.opExtrude","CAP_EDGE",EDGE,{"disambiguationData":[OSD([sQuery(id+"F28.wireOp",EDGE,"E11.0.12.0")])],"isStart":false})});
            var Q14;
            {var subQ0=sQuery(id+"F11.wireOp",EDGE,"E1.right");var subQ1=sQuery(id+"F28.wireOp",EDGE,"E11.0.7.0");Q14=makeQuery(id+"F29.boolean.opBoolean","COPY",EDGE,{"disambiguationData":[TD([makeQuery(id+"F25.opChamfer","BLEND_FACE",FACE,{"disambiguationData":[OSD([subQ0])]})])],"derivedFrom":makeQuery(id+"F29.opExtrude","CAP_EDGE",EDGE,{"disambiguationData":[OSD([subQ1])],"isStart":false})});}
            var Q15;
            {var subQ0=sQuery(id+"F11.wireOp",EDGE,"E1.right");var subQ1=sQuery(id+"F28.wireOp",EDGE,"E11.0.8.0");Q15=makeQuery(id+"F29.boolean.opBoolean","COPY",EDGE,{"disambiguationData":[TD([makeQuery(id+"F25.opChamfer","BLEND_FACE",FACE,{"disambiguationData":[OSD([subQ0])]})])],"derivedFrom":makeQuery(id+"F29.opExtrude","CAP_EDGE",EDGE,{"disambiguationData":[OSD([subQ1])],"isStart":false})});}
            var Q16;
            {var subQ0=sQuery(id+"F11.wireOp",EDGE,"E1.top");var subQ1=sQuery(id+"F28.wireOp",EDGE,"E11.0.9.0");Q16=makeQuery(id+"F29.boolean.opBoolean","COPY",EDGE,{"disambiguationData":[TD([makeQuery(id+"F25.opChamfer","BLEND_FACE",FACE,{"disambiguationData":[OSD([subQ0])]})])],"derivedFrom":makeQuery(id+"F29.opExtrude","CAP_EDGE",EDGE,{"disambiguationData":[OSD([subQ1])],"isStart":false})});}
            var Q17;
            {var subQ0=sQuery(id+"F11.wireOp",EDGE,"E1.top");var subQ1=sQuery(id+"F28.wireOp",EDGE,"E11.0.10.0");Q17=makeQuery(id+"F29.boolean.opBoolean","COPY",EDGE,{"disambiguationData":[TD([makeQuery(id+"F25.opChamfer","BLEND_FACE",FACE,{"disambiguationData":[OSD([subQ0])]})])],"derivedFrom":makeQuery(id+"F29.opExtrude","CAP_EDGE",EDGE,{"disambiguationData":[OSD([subQ1])],"isStart":false})});}
            var Q18;
            {var subQ0=sQuery(id+"F11.wireOp",EDGE,"E1.top");var subQ1=sQuery(id+"F28.wireOp",EDGE,"E11.0.11.0");Q18=makeQuery(id+"F29.boolean.opBoolean","COPY",EDGE,{"disambiguationData":[TD([makeQuery(id+"F25.opChamfer","BLEND_FACE",FACE,{"disambiguationData":[OSD([subQ0])]})])],"derivedFrom":makeQuery(id+"F29.opExtrude","CAP_EDGE",EDGE,{"disambiguationData":[OSD([subQ1])],"isStart":false})});}
            var Q19;
            Q19=makeQuery(id+"F29.boolean.opBoolean","COPY",EDGE,{"derivedFrom":makeQuery(id+"F29.opExtrude","CAP_EDGE",EDGE,{"disambiguationData":[OSD([sQuery(id+"F28.wireOp",EDGE,"E11.0.12.1")])],"isStart":false})});
            var Q20;
            {var subQ0=sQuery(id+"F11.wireOp",EDGE,"E1.top");var subQ1=sQuery(id+"F28.wireOp",EDGE,"E11.0.11.1");Q20=makeQuery(id+"F29.boolean.opBoolean","COPY",EDGE,{"disambiguationData":[TD([makeQuery(id+"F25.opChamfer","BLEND_FACE",FACE,{"disambiguationData":[OSD([subQ0])]})])],"derivedFrom":makeQuery(id+"F29.opExtrude","CAP_EDGE",EDGE,{"disambiguationData":[OSD([subQ1])],"isStart":false})});}
            var Q21;
            {var subQ0=sQuery(id+"F11.wireOp",EDGE,"E1.top");var subQ1=sQuery(id+"F28.wireOp",EDGE,"E11.0.10.1");Q21=makeQuery(id+"F29.boolean.opBoolean","COPY",EDGE,{"disambiguationData":[TD([makeQuery(id+"F25.opChamfer","BLEND_FACE",FACE,{"disambiguationData":[OSD([subQ0])]})])],"derivedFrom":makeQuery(id+"F29.opExtrude","CAP_EDGE",EDGE,{"disambiguationData":[OSD([subQ1])],"isStart":false})});}
            var Q22;
            {var subQ0=sQuery(id+"F11.wireOp",EDGE,"E1.top");var subQ1=sQuery(id+"F28.wireOp",EDGE,"E11.0.9.1");Q22=makeQuery(id+"F29.boolean.opBoolean","COPY",EDGE,{"disambiguationData":[TD([makeQuery(id+"F25.opChamfer","BLEND_FACE",FACE,{"disambiguationData":[OSD([subQ0])]})])],"derivedFrom":makeQuery(id+"F29.opExtrude","CAP_EDGE",EDGE,{"disambiguationData":[OSD([subQ1])],"isStart":false})});}
            var Q23;
            {var subQ0=sQuery(id+"F11.wireOp",EDGE,"E1.right");var subQ1=sQuery(id+"F28.wireOp",EDGE,"E11.0.8.1");Q23=makeQuery(id+"F29.boolean.opBoolean","COPY",EDGE,{"disambiguationData":[TD([makeQuery(id+"F25.opChamfer","BLEND_FACE",FACE,{"disambiguationData":[OSD([subQ0])]})])],"derivedFrom":makeQuery(id+"F29.opExtrude","CAP_EDGE",EDGE,{"disambiguationData":[OSD([subQ1])],"isStart":false})});}
            var Q24;
            {var subQ0=sQuery(id+"F11.wireOp",EDGE,"E1.right");var subQ1=sQuery(id+"F28.wireOp",EDGE,"E11.0.7.1");Q24=makeQuery(id+"F29.boolean.opBoolean","COPY",EDGE,{"disambiguationData":[TD([makeQuery(id+"F25.opChamfer","BLEND_FACE",FACE,{"disambiguationData":[OSD([subQ0])]})])],"derivedFrom":makeQuery(id+"F29.opExtrude","CAP_EDGE",EDGE,{"disambiguationData":[OSD([subQ1])],"isStart":false})});}
            var Q25;
            {var subQ0=sQuery(id+"F11.wireOp",EDGE,"E1.left");var subQ1=sQuery(id+"F28.wireOp",EDGE,"E11.0.11.1");Q25=makeQuery(id+"F29.boolean.opBoolean","COPY",EDGE,{"disambiguationData":[TD([makeQuery(id+"F25.opChamfer","BLEND_FACE",FACE,{"disambiguationData":[OSD([subQ0])]})])],"derivedFrom":makeQuery(id+"F29.opExtrude","CAP_EDGE",EDGE,{"disambiguationData":[OSD([subQ1])],"isStart":false})});}
            var Q26;
            {var subQ0=sQuery(id+"F11.wireOp",EDGE,"E1.right");var subQ1=sQuery(id+"F28.wireOp",EDGE,"E11.0.6.1");Q26=makeQuery(id+"F29.boolean.opBoolean","COPY",EDGE,{"disambiguationData":[TD([makeQuery(id+"F25.opChamfer","BLEND_FACE",FACE,{"disambiguationData":[OSD([subQ0])]}),makeQuery(id+"F26.opChamfer","BLEND_FACE",FACE,{"disambiguationData":[OSD([sQuery(id+"F11.wireOp",EDGE,"E1.bottom"),sQuery(id+"F11.wireOp",EDGE,"E1.top"),sQuery(id+"F11.wireOp",EDGE,"E1.left"),subQ0,sQuery(id+"F18.wireOp",EDGE,"E7")])]}),makeQuery(id+"F29.opExtrude","CAP_FACE",FACE,{"disambiguationData":[OSD([sQuery(id+"F28.wireOp",EDGE,"E11.0.6.0"),subQ1,sQuery(id+"F28.wireOp",EDGE,"E11.0.6.2"),sQuery(id+"F28.wireOp",EDGE,"E11.0.6.3")])],"isStart":false}),makeQuery(id+"F29.opExtrude","SWEPT_FACE",FACE,{"disambiguationData":[OSD([subQ1])]})])],"derivedFrom":makeQuery(id+"F29.opExtrude","CAP_EDGE",EDGE,{"disambiguationData":[OSD([subQ1])],"isStart":false})});}
            var Q27;
            {var subQ0=sQuery(id+"F11.wireOp",EDGE,"E1.left");var subQ1=sQuery(id+"F28.wireOp",EDGE,"E11.0.10.1");Q27=makeQuery(id+"F29.boolean.opBoolean","COPY",EDGE,{"disambiguationData":[TD([makeQuery(id+"F25.opChamfer","BLEND_FACE",FACE,{"disambiguationData":[OSD([subQ0])]})])],"derivedFrom":makeQuery(id+"F29.opExtrude","CAP_EDGE",EDGE,{"disambiguationData":[OSD([subQ1])],"isStart":false})});}
            var Q28;
            {var subQ0=sQuery(id+"F11.wireOp",EDGE,"E1.right");var subQ1=sQuery(id+"F28.wireOp",EDGE,"E11.0.5.1");Q28=makeQuery(id+"F29.boolean.opBoolean","COPY",EDGE,{"disambiguationData":[TD([makeQuery(id+"F25.opChamfer","BLEND_FACE",FACE,{"disambiguationData":[OSD([subQ0])]})])],"derivedFrom":makeQuery(id+"F29.opExtrude","CAP_EDGE",EDGE,{"disambiguationData":[OSD([subQ1])],"isStart":false})});}
            var Q29;
            {var subQ0=sQuery(id+"F11.wireOp",EDGE,"E1.left");var subQ1=sQuery(id+"F28.wireOp",EDGE,"E11.0.9.1");Q29=makeQuery(id+"F29.boolean.opBoolean","COPY",EDGE,{"disambiguationData":[TD([makeQuery(id+"F25.opChamfer","BLEND_FACE",FACE,{"disambiguationData":[OSD([subQ0])]})])],"derivedFrom":makeQuery(id+"F29.opExtrude","CAP_EDGE",EDGE,{"disambiguationData":[OSD([subQ1])],"isStart":false})});}
            var Q30;
            {var subQ0=sQuery(id+"F11.wireOp",EDGE,"E1.left");var subQ1=sQuery(id+"F28.wireOp",EDGE,"E11.0.8.1");Q30=makeQuery(id+"F29.boolean.opBoolean","COPY",EDGE,{"disambiguationData":[TD([makeQuery(id+"F25.opChamfer","BLEND_FACE",FACE,{"disambiguationData":[OSD([subQ0])]})])],"derivedFrom":makeQuery(id+"F29.opExtrude","CAP_EDGE",EDGE,{"disambiguationData":[OSD([subQ1])],"isStart":false})});}
            var Q31;
            {var subQ0=sQuery(id+"F11.wireOp",EDGE,"E1.left");var subQ1=sQuery(id+"F28.wireOp",EDGE,"E11.0.7.1");Q31=makeQuery(id+"F29.boolean.opBoolean","COPY",EDGE,{"disambiguationData":[TD([makeQuery(id+"F25.opChamfer","BLEND_FACE",FACE,{"disambiguationData":[OSD([subQ0])]})])],"derivedFrom":makeQuery(id+"F29.opExtrude","CAP_EDGE",EDGE,{"disambiguationData":[OSD([subQ1])],"isStart":false})});}
            var Q32;
            {var subQ0=sQuery(id+"F11.wireOp",EDGE,"E1.right");var subQ1=sQuery(id+"F11.wireOp",EDGE,"E1.left");var subQ2=sQuery(id+"F11.wireOp",EDGE,"E1.top");var subQ3=sQuery(id+"F11.wireOp",EDGE,"E1.bottom");var subQ4=sQuery(id+"F28.wireOp",EDGE,"E11.0.6.1");Q32=makeQuery(id+"F29.boolean.opBoolean","COPY",EDGE,{"disambiguationData":[TD([makeQuery(id+"F26.opChamfer","BLEND_FACE",FACE,{"disambiguationData":[OSD([subQ3,subQ2,subQ1,subQ0,sQuery(id+"F18.wireOp",EDGE,"E7")])]}),makeQuery(id+"F27.opChamfer","BLEND_FACE",FACE,{"disambiguationData":[OSD([subQ3,subQ2,subQ1,subQ0,sQuery(id+"F22.wireOp",EDGE,"E9")])]}),makeQuery(id+"F29.opExtrude","CAP_FACE",FACE,{"disambiguationData":[OSD([sQuery(id+"F28.wireOp",EDGE,"E11.0.6.0"),subQ4,sQuery(id+"F28.wireOp",EDGE,"E11.0.6.2"),sQuery(id+"F28.wireOp",EDGE,"E11.0.6.3")])],"isStart":false}),makeQuery(id+"F29.opExtrude","SWEPT_FACE",FACE,{"disambiguationData":[OSD([subQ4])]})])],"derivedFrom":makeQuery(id+"F29.opExtrude","CAP_EDGE",EDGE,{"disambiguationData":[OSD([subQ4])],"isStart":false})});}
            var Q33;
            {var subQ0=sQuery(id+"F11.wireOp",EDGE,"E1.right");var subQ1=sQuery(id+"F28.wireOp",EDGE,"E11.0.4.1");Q33=makeQuery(id+"F29.boolean.opBoolean","COPY",EDGE,{"disambiguationData":[TD([makeQuery(id+"F25.opChamfer","BLEND_FACE",FACE,{"disambiguationData":[OSD([subQ0])]})])],"derivedFrom":makeQuery(id+"F29.opExtrude","CAP_EDGE",EDGE,{"disambiguationData":[OSD([subQ1])],"isStart":false})});}
            var Q34;
            {var subQ0=sQuery(id+"F11.wireOp",EDGE,"E1.right");var subQ1=sQuery(id+"F28.wireOp",EDGE,"E11.0.3.1");Q34=makeQuery(id+"F29.boolean.opBoolean","COPY",EDGE,{"disambiguationData":[TD([makeQuery(id+"F25.opChamfer","BLEND_FACE",FACE,{"disambiguationData":[OSD([subQ0])]})])],"derivedFrom":makeQuery(id+"F29.opExtrude","CAP_EDGE",EDGE,{"disambiguationData":[OSD([subQ1])],"isStart":false})});}
            var Q35;
            {var subQ0=sQuery(id+"F11.wireOp",EDGE,"E1.left");var subQ1=sQuery(id+"F28.wireOp",EDGE,"E11.0.6.1");Q35=makeQuery(id+"F29.boolean.opBoolean","COPY",EDGE,{"disambiguationData":[TD([makeQuery(id+"F25.opChamfer","BLEND_FACE",FACE,{"disambiguationData":[OSD([subQ0])]}),makeQuery(id+"F27.opChamfer","BLEND_FACE",FACE,{"disambiguationData":[OSD([sQuery(id+"F11.wireOp",EDGE,"E1.bottom"),sQuery(id+"F11.wireOp",EDGE,"E1.top"),subQ0,sQuery(id+"F11.wireOp",EDGE,"E1.right"),sQuery(id+"F22.wireOp",EDGE,"E9")])]}),makeQuery(id+"F29.opExtrude","CAP_FACE",FACE,{"disambiguationData":[OSD([sQuery(id+"F28.wireOp",EDGE,"E11.0.6.0"),subQ1,sQuery(id+"F28.wireOp",EDGE,"E11.0.6.2"),sQuery(id+"F28.wireOp",EDGE,"E11.0.6.3")])],"isStart":false}),makeQuery(id+"F29.opExtrude","SWEPT_FACE",FACE,{"disambiguationData":[OSD([subQ1])]})])],"derivedFrom":makeQuery(id+"F29.opExtrude","CAP_EDGE",EDGE,{"disambiguationData":[OSD([subQ1])],"isStart":false})});}
            var Q36;
            {var subQ0=sQuery(id+"F11.wireOp",EDGE,"E1.bottom");var subQ1=sQuery(id+"F28.wireOp",EDGE,"E11.0.5.1");Q36=makeQuery(id+"F29.boolean.opBoolean","COPY",EDGE,{"disambiguationData":[TD([makeQuery(id+"F25.opChamfer","BLEND_FACE",FACE,{"disambiguationData":[OSD([subQ0])]})])],"derivedFrom":makeQuery(id+"F29.opExtrude","CAP_EDGE",EDGE,{"disambiguationData":[OSD([subQ1])],"isStart":false})});}
            var Q37;
            {var subQ0=sQuery(id+"F11.wireOp",EDGE,"E1.bottom");var subQ1=sQuery(id+"F28.wireOp",EDGE,"E11.0.4.1");Q37=makeQuery(id+"F29.boolean.opBoolean","COPY",EDGE,{"disambiguationData":[TD([makeQuery(id+"F25.opChamfer","BLEND_FACE",FACE,{"disambiguationData":[OSD([subQ0])]})])],"derivedFrom":makeQuery(id+"F29.opExtrude","CAP_EDGE",EDGE,{"disambiguationData":[OSD([subQ1])],"isStart":false})});}
            var Q38;
            {var subQ0=sQuery(id+"F11.wireOp",EDGE,"E1.bottom");var subQ1=sQuery(id+"F28.wireOp",EDGE,"E11.0.3.1");Q38=makeQuery(id+"F29.boolean.opBoolean","COPY",EDGE,{"disambiguationData":[TD([makeQuery(id+"F25.opChamfer","BLEND_FACE",FACE,{"disambiguationData":[OSD([subQ0])]})])],"derivedFrom":makeQuery(id+"F29.opExtrude","CAP_EDGE",EDGE,{"disambiguationData":[OSD([subQ1])],"isStart":false})});}
            var Q39;
            Q39=makeQuery(id+"F29.boolean.opBoolean","COPY",EDGE,{"derivedFrom":makeQuery(id+"F29.opExtrude","CAP_EDGE",EDGE,{"disambiguationData":[OSD([sQuery(id+"F28.wireOp",EDGE,"E11.0.2.0")])],"isStart":false})});
            var Q40;
            Q40=makeQuery(id+"F29.boolean.opBoolean","COPY",EDGE,{"derivedFrom":makeQuery(id+"F29.opExtrude","CAP_EDGE",EDGE,{"disambiguationData":[OSD([sQuery(id+"F28.wireOp",EDGE,"E11.0.2.1")])],"isStart":false})});
            fillet(context, id + "F30", {"entities" : qUnion([Q0, Q1, Q2, Q3, Q4, Q5, Q6, Q7, Q8, Q9, Q10, Q11, Q12, Q13, Q14, Q15, Q16, Q17, Q18, Q19, Q20, Q21, Q22, Q23, Q24, Q25, Q26, Q27, Q28, Q29, Q30, Q31, Q32, Q33, Q34, Q35, Q36, Q37, Q38, Q39, Q40]), "radius" : 12 * mm, "allowEdgeOverflow" : false});
        }
        {
            var Q0;
            {var subQ0=sQuery(id+"F11.wireOp",EDGE,"E1.bottom");var subQ1=sQuery(id+"F28.wireOp",EDGE,"E11.0.2.0");var subQ2=sQuery(id+"F11.wireOp",EDGE,"E1.right");Q0=makeQuery(id+"F30.opFillet","BLEND_EDGE",EDGE,{"blendedFrom":[makeQuery(id+"F29.boolean.opBoolean","COPY",EDGE,{"derivedFrom":makeQuery(id+"F29.opExtrude","CAP_EDGE",EDGE,{"disambiguationData":[OSD([subQ1])],"isStart":false})}),makeQuery(id+"F29.boolean.opBoolean","SPLIT",FACE,{"disambiguationData":[TD([makeQuery(id+"F25.opChamfer","BLEND_FACE",FACE,{"disambiguationData":[OSD([subQ0])]}),makeQuery(id+"F25.opChamfer","BLEND_FACE",FACE,{"disambiguationData":[OSD([subQ2])]}),makeQuery(id+"F29.opExtrude","SWEPT_FACE",FACE,{"disambiguationData":[OSD([subQ1])]})])],"derivedFrom":makeQuery(id+"F12.opExtrude","CAP_FACE",FACE,{"disambiguationData":[OSD([subQ0,sQuery(id+"F11.wireOp",EDGE,"E1.top"),sQuery(id+"F11.wireOp",EDGE,"E1.left"),subQ2])],"isStart":false})})],"blendedInto":[makeQuery(id+"F29.boolean.opBoolean","SPLIT",FACE,{"disambiguationData":[TD([makeQuery(id+"F25.opChamfer","BLEND_FACE",FACE,{"disambiguationData":[OSD([subQ0])]}),makeQuery(id+"F25.opChamfer","BLEND_FACE",FACE,{"disambiguationData":[OSD([subQ2])]}),makeQuery(id+"F29.opExtrude","SWEPT_FACE",FACE,{"disambiguationData":[OSD([subQ1])]})])],"derivedFrom":makeQuery(id+"F12.opExtrude","CAP_FACE",FACE,{"disambiguationData":[OSD([subQ0,sQuery(id+"F11.wireOp",EDGE,"E1.top"),sQuery(id+"F11.wireOp",EDGE,"E1.left"),subQ2])],"isStart":false})})]});}
            var Q1;
            {var subQ0=sQuery(id+"F11.wireOp",EDGE,"E1.bottom");var subQ1=sQuery(id+"F11.wireOp",EDGE,"E1.right");var subQ2=sQuery(id+"F28.wireOp",EDGE,"E11.0.2.1");Q1=makeQuery(id+"F30.opFillet","BLEND_EDGE",EDGE,{"blendedFrom":[makeQuery(id+"F29.boolean.opBoolean","COPY",EDGE,{"derivedFrom":makeQuery(id+"F29.opExtrude","CAP_EDGE",EDGE,{"disambiguationData":[OSD([subQ2])],"isStart":false})}),makeQuery(id+"F29.boolean.opBoolean","SPLIT",FACE,{"disambiguationData":[TD([makeQuery(id+"F25.opChamfer","BLEND_FACE",FACE,{"disambiguationData":[OSD([subQ0])]}),makeQuery(id+"F25.opChamfer","BLEND_FACE",FACE,{"disambiguationData":[OSD([subQ1])]}),makeQuery(id+"F29.opExtrude","SWEPT_FACE",FACE,{"disambiguationData":[OSD([subQ2])]}),makeQuery(id+"F29.opExtrude","SWEPT_FACE",FACE,{"disambiguationData":[OSD([sQuery(id+"F28.wireOp",EDGE,"E11.0.3.0")])]})])],"derivedFrom":makeQuery(id+"F12.opExtrude","CAP_FACE",FACE,{"disambiguationData":[OSD([subQ0,sQuery(id+"F11.wireOp",EDGE,"E1.top"),sQuery(id+"F11.wireOp",EDGE,"E1.left"),subQ1])],"isStart":false})})],"blendedInto":[makeQuery(id+"F29.boolean.opBoolean","SPLIT",FACE,{"disambiguationData":[TD([makeQuery(id+"F25.opChamfer","BLEND_FACE",FACE,{"disambiguationData":[OSD([subQ0])]}),makeQuery(id+"F25.opChamfer","BLEND_FACE",FACE,{"disambiguationData":[OSD([subQ1])]}),makeQuery(id+"F29.opExtrude","SWEPT_FACE",FACE,{"disambiguationData":[OSD([subQ2])]}),makeQuery(id+"F29.opExtrude","SWEPT_FACE",FACE,{"disambiguationData":[OSD([sQuery(id+"F28.wireOp",EDGE,"E11.0.3.0")])]})])],"derivedFrom":makeQuery(id+"F12.opExtrude","CAP_FACE",FACE,{"disambiguationData":[OSD([subQ0,sQuery(id+"F11.wireOp",EDGE,"E1.top"),sQuery(id+"F11.wireOp",EDGE,"E1.left"),subQ1])],"isStart":false})})]});}
            var Q2;
            {var subQ0=sQuery(id+"F11.wireOp",EDGE,"E1.bottom");var subQ1=sQuery(id+"F11.wireOp",EDGE,"E1.right");var subQ2=sQuery(id+"F28.wireOp",EDGE,"E11.0.3.0");Q2=makeQuery(id+"F30.opFillet","BLEND_EDGE",EDGE,{"blendedFrom":[makeQuery(id+"F29.boolean.opBoolean","COPY",EDGE,{"derivedFrom":makeQuery(id+"F29.opExtrude","CAP_EDGE",EDGE,{"disambiguationData":[OSD([subQ2])],"isStart":false})}),makeQuery(id+"F29.boolean.opBoolean","SPLIT",FACE,{"disambiguationData":[TD([makeQuery(id+"F25.opChamfer","BLEND_FACE",FACE,{"disambiguationData":[OSD([subQ0])]}),makeQuery(id+"F25.opChamfer","BLEND_FACE",FACE,{"disambiguationData":[OSD([subQ1])]}),makeQuery(id+"F29.opExtrude","SWEPT_FACE",FACE,{"disambiguationData":[OSD([sQuery(id+"F28.wireOp",EDGE,"E11.0.2.1")])]}),makeQuery(id+"F29.opExtrude","SWEPT_FACE",FACE,{"disambiguationData":[OSD([subQ2])]})])],"derivedFrom":makeQuery(id+"F12.opExtrude","CAP_FACE",FACE,{"disambiguationData":[OSD([subQ0,sQuery(id+"F11.wireOp",EDGE,"E1.top"),sQuery(id+"F11.wireOp",EDGE,"E1.left"),subQ1])],"isStart":false})})],"blendedInto":[makeQuery(id+"F29.boolean.opBoolean","SPLIT",FACE,{"disambiguationData":[TD([makeQuery(id+"F25.opChamfer","BLEND_FACE",FACE,{"disambiguationData":[OSD([subQ0])]}),makeQuery(id+"F25.opChamfer","BLEND_FACE",FACE,{"disambiguationData":[OSD([subQ1])]}),makeQuery(id+"F29.opExtrude","SWEPT_FACE",FACE,{"disambiguationData":[OSD([sQuery(id+"F28.wireOp",EDGE,"E11.0.2.1")])]}),makeQuery(id+"F29.opExtrude","SWEPT_FACE",FACE,{"disambiguationData":[OSD([subQ2])]})])],"derivedFrom":makeQuery(id+"F12.opExtrude","CAP_FACE",FACE,{"disambiguationData":[OSD([subQ0,sQuery(id+"F11.wireOp",EDGE,"E1.top"),sQuery(id+"F11.wireOp",EDGE,"E1.left"),subQ1])],"isStart":false})})]});}
            var Q3;
            {var subQ0=sQuery(id+"F11.wireOp",EDGE,"E1.right");var subQ1=sQuery(id+"F11.wireOp",EDGE,"E1.left");var subQ2=sQuery(id+"F11.wireOp",EDGE,"E1.top");var subQ3=sQuery(id+"F11.wireOp",EDGE,"E1.bottom");var subQ4=makeQuery(id+"F27.opChamfer","BLEND_FACE",FACE,{"disambiguationData":[OSD([subQ3,subQ2,subQ1,subQ0,sQuery(id+"F22.wireOp",EDGE,"E9")])]});var subQ5=sQuery(id+"F28.wireOp",EDGE,"E11.0.3.1");var subQ6=makeQuery(id+"F29.opExtrude","SWEPT_FACE",FACE,{"disambiguationData":[OSD([subQ5])]});Q3=makeQuery(id+"F30.opFillet","BLEND_EDGE",EDGE,{"blendedFrom":[makeQuery(id+"F29.boolean.opBoolean","COPY",EDGE,{"disambiguationData":[TD([makeQuery(id+"F25.opChamfer","BLEND_FACE",FACE,{"disambiguationData":[OSD([subQ3])]})])],"derivedFrom":makeQuery(id+"F29.opExtrude","CAP_EDGE",EDGE,{"disambiguationData":[OSD([subQ5])],"isStart":false})}),makeQuery(id+"F29.boolean.opBoolean","SPLIT",FACE,{"disambiguationData":[TD([makeQuery(id+"F25.opChamfer","BLEND_FACE",FACE,{"disambiguationData":[OSD([subQ0])]}),subQ4,subQ6,makeQuery(id+"F29.opExtrude","SWEPT_FACE",FACE,{"disambiguationData":[OSD([sQuery(id+"F28.wireOp",EDGE,"E11.0.4.0")])]})])],"derivedFrom":makeQuery(id+"F12.opExtrude","CAP_FACE",FACE,{"disambiguationData":[OSD([subQ3,subQ2,subQ1,subQ0])],"isStart":false})})],"blendedInto":[makeQuery(id+"F29.boolean.opBoolean","SPLIT",FACE,{"disambiguationData":[TD([makeQuery(id+"F25.opChamfer","BLEND_FACE",FACE,{"disambiguationData":[OSD([subQ0])]}),subQ4,subQ6,makeQuery(id+"F29.opExtrude","SWEPT_FACE",FACE,{"disambiguationData":[OSD([sQuery(id+"F28.wireOp",EDGE,"E11.0.4.0")])]})])],"derivedFrom":makeQuery(id+"F12.opExtrude","CAP_FACE",FACE,{"disambiguationData":[OSD([subQ3,subQ2,subQ1,subQ0])],"isStart":false})})]});}
            var Q4;
            {var subQ0=sQuery(id+"F11.wireOp",EDGE,"E1.right");var subQ1=makeQuery(id+"F25.opChamfer","BLEND_FACE",FACE,{"disambiguationData":[OSD([subQ0])]});var subQ2=sQuery(id+"F11.wireOp",EDGE,"E1.left");var subQ3=sQuery(id+"F11.wireOp",EDGE,"E1.top");var subQ4=sQuery(id+"F11.wireOp",EDGE,"E1.bottom");var subQ5=makeQuery(id+"F27.opChamfer","BLEND_FACE",FACE,{"disambiguationData":[OSD([subQ4,subQ3,subQ2,subQ0,sQuery(id+"F22.wireOp",EDGE,"E9")])]});var subQ6=sQuery(id+"F28.wireOp",EDGE,"E11.0.4.0");var subQ7=makeQuery(id+"F29.opExtrude","SWEPT_FACE",FACE,{"disambiguationData":[OSD([subQ6])]});Q4=makeQuery(id+"F30.opFillet","BLEND_EDGE",EDGE,{"blendedFrom":[makeQuery(id+"F29.boolean.opBoolean","COPY",EDGE,{"disambiguationData":[TD([subQ1])],"derivedFrom":makeQuery(id+"F29.opExtrude","CAP_EDGE",EDGE,{"disambiguationData":[OSD([subQ6])],"isStart":false})}),makeQuery(id+"F29.boolean.opBoolean","SPLIT",FACE,{"disambiguationData":[TD([subQ1,subQ5,makeQuery(id+"F29.opExtrude","SWEPT_FACE",FACE,{"disambiguationData":[OSD([sQuery(id+"F28.wireOp",EDGE,"E11.0.3.1")])]}),subQ7])],"derivedFrom":makeQuery(id+"F12.opExtrude","CAP_FACE",FACE,{"disambiguationData":[OSD([subQ4,subQ3,subQ2,subQ0])],"isStart":false})})],"blendedInto":[makeQuery(id+"F29.boolean.opBoolean","SPLIT",FACE,{"disambiguationData":[TD([subQ1,subQ5,makeQuery(id+"F29.opExtrude","SWEPT_FACE",FACE,{"disambiguationData":[OSD([sQuery(id+"F28.wireOp",EDGE,"E11.0.3.1")])]}),subQ7])],"derivedFrom":makeQuery(id+"F12.opExtrude","CAP_FACE",FACE,{"disambiguationData":[OSD([subQ4,subQ3,subQ2,subQ0])],"isStart":false})})]});}
            var Q5;
            {var subQ0=sQuery(id+"F11.wireOp",EDGE,"E1.right");var subQ1=makeQuery(id+"F25.opChamfer","BLEND_FACE",FACE,{"disambiguationData":[OSD([subQ0])]});var subQ2=sQuery(id+"F28.wireOp",EDGE,"E11.0.5.0");var subQ3=makeQuery(id+"F29.opExtrude","SWEPT_FACE",FACE,{"disambiguationData":[OSD([subQ2])]});var subQ4=sQuery(id+"F11.wireOp",EDGE,"E1.left");var subQ5=sQuery(id+"F11.wireOp",EDGE,"E1.top");var subQ6=sQuery(id+"F11.wireOp",EDGE,"E1.bottom");var subQ7=makeQuery(id+"F27.opChamfer","BLEND_FACE",FACE,{"disambiguationData":[OSD([subQ6,subQ5,subQ4,subQ0,sQuery(id+"F22.wireOp",EDGE,"E9")])]});Q5=makeQuery(id+"F30.opFillet","BLEND_EDGE",EDGE,{"blendedFrom":[makeQuery(id+"F29.boolean.opBoolean","COPY",EDGE,{"disambiguationData":[TD([subQ1])],"derivedFrom":makeQuery(id+"F29.opExtrude","CAP_EDGE",EDGE,{"disambiguationData":[OSD([subQ2])],"isStart":false})}),makeQuery(id+"F29.boolean.opBoolean","SPLIT",FACE,{"disambiguationData":[TD([subQ1,subQ7,makeQuery(id+"F29.opExtrude","SWEPT_FACE",FACE,{"disambiguationData":[OSD([sQuery(id+"F28.wireOp",EDGE,"E11.0.4.1")])]}),subQ3])],"derivedFrom":makeQuery(id+"F12.opExtrude","CAP_FACE",FACE,{"disambiguationData":[OSD([subQ6,subQ5,subQ4,subQ0])],"isStart":false})})],"blendedInto":[makeQuery(id+"F29.boolean.opBoolean","SPLIT",FACE,{"disambiguationData":[TD([subQ1,subQ7,makeQuery(id+"F29.opExtrude","SWEPT_FACE",FACE,{"disambiguationData":[OSD([sQuery(id+"F28.wireOp",EDGE,"E11.0.4.1")])]}),subQ3])],"derivedFrom":makeQuery(id+"F12.opExtrude","CAP_FACE",FACE,{"disambiguationData":[OSD([subQ6,subQ5,subQ4,subQ0])],"isStart":false})})]});}
            var Q6;
            {var subQ0=sQuery(id+"F11.wireOp",EDGE,"E1.right");var subQ1=sQuery(id+"F11.wireOp",EDGE,"E1.left");var subQ2=sQuery(id+"F11.wireOp",EDGE,"E1.top");var subQ3=sQuery(id+"F11.wireOp",EDGE,"E1.bottom");var subQ4=makeQuery(id+"F27.opChamfer","BLEND_FACE",FACE,{"disambiguationData":[OSD([subQ3,subQ2,subQ1,subQ0,sQuery(id+"F22.wireOp",EDGE,"E9")])]});var subQ5=sQuery(id+"F28.wireOp",EDGE,"E11.0.5.1");var subQ6=makeQuery(id+"F29.opExtrude","SWEPT_FACE",FACE,{"disambiguationData":[OSD([subQ5])]});var subQ7=makeQuery(id+"F25.opChamfer","BLEND_FACE",FACE,{"disambiguationData":[OSD([subQ0])]});Q6=makeQuery(id+"F30.opFillet","BLEND_EDGE",EDGE,{"blendedFrom":[makeQuery(id+"F29.boolean.opBoolean","COPY",EDGE,{"disambiguationData":[TD([subQ7])],"derivedFrom":makeQuery(id+"F29.opExtrude","CAP_EDGE",EDGE,{"disambiguationData":[OSD([subQ5])],"isStart":false})}),makeQuery(id+"F29.boolean.opBoolean","SPLIT",FACE,{"disambiguationData":[TD([subQ7,makeQuery(id+"F26.opChamfer","BLEND_FACE",FACE,{"disambiguationData":[OSD([subQ3,subQ2,subQ1,subQ0,sQuery(id+"F18.wireOp",EDGE,"E7")])]}),subQ4,subQ6,makeQuery(id+"F29.opExtrude","SWEPT_FACE",FACE,{"disambiguationData":[OSD([sQuery(id+"F28.wireOp",EDGE,"E11.0.6.0")])]})])],"derivedFrom":makeQuery(id+"F12.opExtrude","CAP_FACE",FACE,{"disambiguationData":[OSD([subQ3,subQ2,subQ1,subQ0])],"isStart":false})})],"blendedInto":[makeQuery(id+"F29.boolean.opBoolean","SPLIT",FACE,{"disambiguationData":[TD([subQ7,makeQuery(id+"F26.opChamfer","BLEND_FACE",FACE,{"disambiguationData":[OSD([subQ3,subQ2,subQ1,subQ0,sQuery(id+"F18.wireOp",EDGE,"E7")])]}),subQ4,subQ6,makeQuery(id+"F29.opExtrude","SWEPT_FACE",FACE,{"disambiguationData":[OSD([sQuery(id+"F28.wireOp",EDGE,"E11.0.6.0")])]})])],"derivedFrom":makeQuery(id+"F12.opExtrude","CAP_FACE",FACE,{"disambiguationData":[OSD([subQ3,subQ2,subQ1,subQ0])],"isStart":false})})]});}
            var Q7;
            {var subQ0=sQuery(id+"F11.wireOp",EDGE,"E1.right");var subQ1=sQuery(id+"F11.wireOp",EDGE,"E1.left");var subQ2=sQuery(id+"F11.wireOp",EDGE,"E1.top");var subQ3=sQuery(id+"F11.wireOp",EDGE,"E1.bottom");var subQ4=makeQuery(id+"F26.opChamfer","BLEND_FACE",FACE,{"disambiguationData":[OSD([subQ3,subQ2,subQ1,subQ0,sQuery(id+"F18.wireOp",EDGE,"E7")])]});var subQ5=makeQuery(id+"F25.opChamfer","BLEND_FACE",FACE,{"disambiguationData":[OSD([subQ0])]});var subQ6=sQuery(id+"F28.wireOp",EDGE,"E11.0.6.0");var subQ7=makeQuery(id+"F29.opExtrude","SWEPT_FACE",FACE,{"disambiguationData":[OSD([subQ6])]});Q7=makeQuery(id+"F30.opFillet","BLEND_EDGE",EDGE,{"blendedFrom":[makeQuery(id+"F29.boolean.opBoolean","COPY",EDGE,{"disambiguationData":[TD([subQ5,subQ4,subQ7,makeQuery(id+"F29.opExtrude","CAP_FACE",FACE,{"disambiguationData":[OSD([subQ6,sQuery(id+"F28.wireOp",EDGE,"E11.0.6.1"),sQuery(id+"F28.wireOp",EDGE,"E11.0.6.2"),sQuery(id+"F28.wireOp",EDGE,"E11.0.6.3")])],"isStart":false})])],"derivedFrom":makeQuery(id+"F29.opExtrude","CAP_EDGE",EDGE,{"disambiguationData":[OSD([subQ6])],"isStart":false})}),makeQuery(id+"F29.boolean.opBoolean","SPLIT",FACE,{"disambiguationData":[TD([subQ5,subQ4,makeQuery(id+"F27.opChamfer","BLEND_FACE",FACE,{"disambiguationData":[OSD([subQ3,subQ2,subQ1,subQ0,sQuery(id+"F22.wireOp",EDGE,"E9")])]}),makeQuery(id+"F29.opExtrude","SWEPT_FACE",FACE,{"disambiguationData":[OSD([sQuery(id+"F28.wireOp",EDGE,"E11.0.5.1")])]}),subQ7])],"derivedFrom":makeQuery(id+"F12.opExtrude","CAP_FACE",FACE,{"disambiguationData":[OSD([subQ3,subQ2,subQ1,subQ0])],"isStart":false})})],"blendedInto":[makeQuery(id+"F29.boolean.opBoolean","SPLIT",FACE,{"disambiguationData":[TD([subQ5,subQ4,makeQuery(id+"F27.opChamfer","BLEND_FACE",FACE,{"disambiguationData":[OSD([subQ3,subQ2,subQ1,subQ0,sQuery(id+"F22.wireOp",EDGE,"E9")])]}),makeQuery(id+"F29.opExtrude","SWEPT_FACE",FACE,{"disambiguationData":[OSD([sQuery(id+"F28.wireOp",EDGE,"E11.0.5.1")])]}),subQ7])],"derivedFrom":makeQuery(id+"F12.opExtrude","CAP_FACE",FACE,{"disambiguationData":[OSD([subQ3,subQ2,subQ1,subQ0])],"isStart":false})})]});}
            var Q8;
            {var subQ0=sQuery(id+"F11.wireOp",EDGE,"E1.right");var subQ1=makeQuery(id+"F25.opChamfer","BLEND_FACE",FACE,{"disambiguationData":[OSD([subQ0])]});var subQ2=sQuery(id+"F11.wireOp",EDGE,"E1.left");var subQ3=sQuery(id+"F11.wireOp",EDGE,"E1.top");var subQ4=sQuery(id+"F11.wireOp",EDGE,"E1.bottom");var subQ5=makeQuery(id+"F26.opChamfer","BLEND_FACE",FACE,{"disambiguationData":[OSD([subQ4,subQ3,subQ2,subQ0,sQuery(id+"F18.wireOp",EDGE,"E7")])]});var subQ6=sQuery(id+"F28.wireOp",EDGE,"E11.0.6.1");var subQ7=makeQuery(id+"F29.opExtrude","SWEPT_FACE",FACE,{"disambiguationData":[OSD([subQ6])]});Q8=makeQuery(id+"F30.opFillet","BLEND_EDGE",EDGE,{"blendedFrom":[makeQuery(id+"F29.boolean.opBoolean","COPY",EDGE,{"disambiguationData":[TD([subQ1,subQ5,makeQuery(id+"F29.opExtrude","CAP_FACE",FACE,{"disambiguationData":[OSD([sQuery(id+"F28.wireOp",EDGE,"E11.0.6.0"),subQ6,sQuery(id+"F28.wireOp",EDGE,"E11.0.6.2"),sQuery(id+"F28.wireOp",EDGE,"E11.0.6.3")])],"isStart":false}),subQ7])],"derivedFrom":makeQuery(id+"F29.opExtrude","CAP_EDGE",EDGE,{"disambiguationData":[OSD([subQ6])],"isStart":false})}),makeQuery(id+"F29.boolean.opBoolean","SPLIT",FACE,{"disambiguationData":[TD([subQ1,subQ5,subQ7,makeQuery(id+"F29.opExtrude","SWEPT_FACE",FACE,{"disambiguationData":[OSD([sQuery(id+"F28.wireOp",EDGE,"E11.0.7.0")])]})])],"derivedFrom":makeQuery(id+"F12.opExtrude","CAP_FACE",FACE,{"disambiguationData":[OSD([subQ4,subQ3,subQ2,subQ0])],"isStart":false})})],"blendedInto":[makeQuery(id+"F29.boolean.opBoolean","SPLIT",FACE,{"disambiguationData":[TD([subQ1,subQ5,subQ7,makeQuery(id+"F29.opExtrude","SWEPT_FACE",FACE,{"disambiguationData":[OSD([sQuery(id+"F28.wireOp",EDGE,"E11.0.7.0")])]})])],"derivedFrom":makeQuery(id+"F12.opExtrude","CAP_FACE",FACE,{"disambiguationData":[OSD([subQ4,subQ3,subQ2,subQ0])],"isStart":false})})]});}
            var Q9;
            {var subQ0=sQuery(id+"F11.wireOp",EDGE,"E1.right");var subQ1=makeQuery(id+"F25.opChamfer","BLEND_FACE",FACE,{"disambiguationData":[OSD([subQ0])]});var subQ2=sQuery(id+"F11.wireOp",EDGE,"E1.left");var subQ3=sQuery(id+"F11.wireOp",EDGE,"E1.top");var subQ4=sQuery(id+"F11.wireOp",EDGE,"E1.bottom");var subQ5=makeQuery(id+"F26.opChamfer","BLEND_FACE",FACE,{"disambiguationData":[OSD([subQ4,subQ3,subQ2,subQ0,sQuery(id+"F18.wireOp",EDGE,"E7")])]});var subQ6=sQuery(id+"F28.wireOp",EDGE,"E11.0.7.0");var subQ7=makeQuery(id+"F29.opExtrude","SWEPT_FACE",FACE,{"disambiguationData":[OSD([subQ6])]});Q9=makeQuery(id+"F30.opFillet","BLEND_EDGE",EDGE,{"blendedFrom":[makeQuery(id+"F29.boolean.opBoolean","COPY",EDGE,{"disambiguationData":[TD([subQ1])],"derivedFrom":makeQuery(id+"F29.opExtrude","CAP_EDGE",EDGE,{"disambiguationData":[OSD([subQ6])],"isStart":false})}),makeQuery(id+"F29.boolean.opBoolean","SPLIT",FACE,{"disambiguationData":[TD([subQ1,subQ5,makeQuery(id+"F29.opExtrude","SWEPT_FACE",FACE,{"disambiguationData":[OSD([sQuery(id+"F28.wireOp",EDGE,"E11.0.6.1")])]}),subQ7])],"derivedFrom":makeQuery(id+"F12.opExtrude","CAP_FACE",FACE,{"disambiguationData":[OSD([subQ4,subQ3,subQ2,subQ0])],"isStart":false})})],"blendedInto":[makeQuery(id+"F29.boolean.opBoolean","SPLIT",FACE,{"disambiguationData":[TD([subQ1,subQ5,makeQuery(id+"F29.opExtrude","SWEPT_FACE",FACE,{"disambiguationData":[OSD([sQuery(id+"F28.wireOp",EDGE,"E11.0.6.1")])]}),subQ7])],"derivedFrom":makeQuery(id+"F12.opExtrude","CAP_FACE",FACE,{"disambiguationData":[OSD([subQ4,subQ3,subQ2,subQ0])],"isStart":false})})]});}
            var Q10;
            {var subQ0=sQuery(id+"F11.wireOp",EDGE,"E1.right");var subQ1=makeQuery(id+"F25.opChamfer","BLEND_FACE",FACE,{"disambiguationData":[OSD([subQ0])]});var subQ2=sQuery(id+"F28.wireOp",EDGE,"E11.0.7.1");var subQ3=makeQuery(id+"F29.opExtrude","SWEPT_FACE",FACE,{"disambiguationData":[OSD([subQ2])]});var subQ4=sQuery(id+"F11.wireOp",EDGE,"E1.left");var subQ5=sQuery(id+"F11.wireOp",EDGE,"E1.top");var subQ6=sQuery(id+"F11.wireOp",EDGE,"E1.bottom");var subQ7=makeQuery(id+"F26.opChamfer","BLEND_FACE",FACE,{"disambiguationData":[OSD([subQ6,subQ5,subQ4,subQ0,sQuery(id+"F18.wireOp",EDGE,"E7")])]});Q10=makeQuery(id+"F30.opFillet","BLEND_EDGE",EDGE,{"blendedFrom":[makeQuery(id+"F29.boolean.opBoolean","COPY",EDGE,{"disambiguationData":[TD([subQ1])],"derivedFrom":makeQuery(id+"F29.opExtrude","CAP_EDGE",EDGE,{"disambiguationData":[OSD([subQ2])],"isStart":false})}),makeQuery(id+"F29.boolean.opBoolean","SPLIT",FACE,{"disambiguationData":[TD([subQ1,subQ7,subQ3,makeQuery(id+"F29.opExtrude","SWEPT_FACE",FACE,{"disambiguationData":[OSD([sQuery(id+"F28.wireOp",EDGE,"E11.0.8.0")])]})])],"derivedFrom":makeQuery(id+"F12.opExtrude","CAP_FACE",FACE,{"disambiguationData":[OSD([subQ6,subQ5,subQ4,subQ0])],"isStart":false})})],"blendedInto":[makeQuery(id+"F29.boolean.opBoolean","SPLIT",FACE,{"disambiguationData":[TD([subQ1,subQ7,subQ3,makeQuery(id+"F29.opExtrude","SWEPT_FACE",FACE,{"disambiguationData":[OSD([sQuery(id+"F28.wireOp",EDGE,"E11.0.8.0")])]})])],"derivedFrom":makeQuery(id+"F12.opExtrude","CAP_FACE",FACE,{"disambiguationData":[OSD([subQ6,subQ5,subQ4,subQ0])],"isStart":false})})]});}
            var Q11;
            {var subQ0=sQuery(id+"F11.wireOp",EDGE,"E1.right");var subQ1=makeQuery(id+"F25.opChamfer","BLEND_FACE",FACE,{"disambiguationData":[OSD([subQ0])]});var subQ2=sQuery(id+"F11.wireOp",EDGE,"E1.left");var subQ3=sQuery(id+"F11.wireOp",EDGE,"E1.top");var subQ4=sQuery(id+"F11.wireOp",EDGE,"E1.bottom");var subQ5=makeQuery(id+"F26.opChamfer","BLEND_FACE",FACE,{"disambiguationData":[OSD([subQ4,subQ3,subQ2,subQ0,sQuery(id+"F18.wireOp",EDGE,"E7")])]});var subQ6=sQuery(id+"F28.wireOp",EDGE,"E11.0.8.0");var subQ7=makeQuery(id+"F29.opExtrude","SWEPT_FACE",FACE,{"disambiguationData":[OSD([subQ6])]});Q11=makeQuery(id+"F30.opFillet","BLEND_EDGE",EDGE,{"blendedFrom":[makeQuery(id+"F29.boolean.opBoolean","COPY",EDGE,{"disambiguationData":[TD([subQ1])],"derivedFrom":makeQuery(id+"F29.opExtrude","CAP_EDGE",EDGE,{"disambiguationData":[OSD([subQ6])],"isStart":false})}),makeQuery(id+"F29.boolean.opBoolean","SPLIT",FACE,{"disambiguationData":[TD([subQ1,subQ5,makeQuery(id+"F29.opExtrude","SWEPT_FACE",FACE,{"disambiguationData":[OSD([sQuery(id+"F28.wireOp",EDGE,"E11.0.7.1")])]}),subQ7])],"derivedFrom":makeQuery(id+"F12.opExtrude","CAP_FACE",FACE,{"disambiguationData":[OSD([subQ4,subQ3,subQ2,subQ0])],"isStart":false})})],"blendedInto":[makeQuery(id+"F29.boolean.opBoolean","SPLIT",FACE,{"disambiguationData":[TD([subQ1,subQ5,makeQuery(id+"F29.opExtrude","SWEPT_FACE",FACE,{"disambiguationData":[OSD([sQuery(id+"F28.wireOp",EDGE,"E11.0.7.1")])]}),subQ7])],"derivedFrom":makeQuery(id+"F12.opExtrude","CAP_FACE",FACE,{"disambiguationData":[OSD([subQ4,subQ3,subQ2,subQ0])],"isStart":false})})]});}
            var Q12;
            {var subQ0=sQuery(id+"F28.wireOp",EDGE,"E11.0.8.1");var subQ1=makeQuery(id+"F29.opExtrude","SWEPT_FACE",FACE,{"disambiguationData":[OSD([subQ0])]});var subQ2=sQuery(id+"F11.wireOp",EDGE,"E1.right");var subQ3=makeQuery(id+"F25.opChamfer","BLEND_FACE",FACE,{"disambiguationData":[OSD([subQ2])]});var subQ4=sQuery(id+"F11.wireOp",EDGE,"E1.left");var subQ5=sQuery(id+"F11.wireOp",EDGE,"E1.top");var subQ6=sQuery(id+"F11.wireOp",EDGE,"E1.bottom");var subQ7=makeQuery(id+"F26.opChamfer","BLEND_FACE",FACE,{"disambiguationData":[OSD([subQ6,subQ5,subQ4,subQ2,sQuery(id+"F18.wireOp",EDGE,"E7")])]});Q12=makeQuery(id+"F30.opFillet","BLEND_EDGE",EDGE,{"blendedFrom":[makeQuery(id+"F29.boolean.opBoolean","COPY",EDGE,{"disambiguationData":[TD([subQ3])],"derivedFrom":makeQuery(id+"F29.opExtrude","CAP_EDGE",EDGE,{"disambiguationData":[OSD([subQ0])],"isStart":false})}),makeQuery(id+"F29.boolean.opBoolean","SPLIT",FACE,{"disambiguationData":[TD([makeQuery(id+"F25.opChamfer","BLEND_FACE",FACE,{"disambiguationData":[OSD([subQ5])]}),subQ3,subQ7,subQ1,makeQuery(id+"F29.opExtrude","SWEPT_FACE",FACE,{"disambiguationData":[OSD([sQuery(id+"F28.wireOp",EDGE,"E11.0.9.0")])]})])],"derivedFrom":makeQuery(id+"F12.opExtrude","CAP_FACE",FACE,{"disambiguationData":[OSD([subQ6,subQ5,subQ4,subQ2])],"isStart":false})})],"blendedInto":[makeQuery(id+"F29.boolean.opBoolean","SPLIT",FACE,{"disambiguationData":[TD([makeQuery(id+"F25.opChamfer","BLEND_FACE",FACE,{"disambiguationData":[OSD([subQ5])]}),subQ3,subQ7,subQ1,makeQuery(id+"F29.opExtrude","SWEPT_FACE",FACE,{"disambiguationData":[OSD([sQuery(id+"F28.wireOp",EDGE,"E11.0.9.0")])]})])],"derivedFrom":makeQuery(id+"F12.opExtrude","CAP_FACE",FACE,{"disambiguationData":[OSD([subQ6,subQ5,subQ4,subQ2])],"isStart":false})})]});}
            var Q13;
            {var subQ0=sQuery(id+"F11.wireOp",EDGE,"E1.right");var subQ1=sQuery(id+"F11.wireOp",EDGE,"E1.left");var subQ2=sQuery(id+"F11.wireOp",EDGE,"E1.top");var subQ3=sQuery(id+"F11.wireOp",EDGE,"E1.bottom");var subQ4=makeQuery(id+"F26.opChamfer","BLEND_FACE",FACE,{"disambiguationData":[OSD([subQ3,subQ2,subQ1,subQ0,sQuery(id+"F18.wireOp",EDGE,"E7")])]});var subQ5=makeQuery(id+"F25.opChamfer","BLEND_FACE",FACE,{"disambiguationData":[OSD([subQ2])]});var subQ6=sQuery(id+"F28.wireOp",EDGE,"E11.0.9.0");var subQ7=makeQuery(id+"F29.opExtrude","SWEPT_FACE",FACE,{"disambiguationData":[OSD([subQ6])]});Q13=makeQuery(id+"F30.opFillet","BLEND_EDGE",EDGE,{"blendedFrom":[makeQuery(id+"F29.boolean.opBoolean","COPY",EDGE,{"disambiguationData":[TD([subQ5])],"derivedFrom":makeQuery(id+"F29.opExtrude","CAP_EDGE",EDGE,{"disambiguationData":[OSD([subQ6])],"isStart":false})}),makeQuery(id+"F29.boolean.opBoolean","SPLIT",FACE,{"disambiguationData":[TD([subQ5,makeQuery(id+"F25.opChamfer","BLEND_FACE",FACE,{"disambiguationData":[OSD([subQ0])]}),subQ4,makeQuery(id+"F29.opExtrude","SWEPT_FACE",FACE,{"disambiguationData":[OSD([sQuery(id+"F28.wireOp",EDGE,"E11.0.8.1")])]}),subQ7])],"derivedFrom":makeQuery(id+"F12.opExtrude","CAP_FACE",FACE,{"disambiguationData":[OSD([subQ3,subQ2,subQ1,subQ0])],"isStart":false})})],"blendedInto":[makeQuery(id+"F29.boolean.opBoolean","SPLIT",FACE,{"disambiguationData":[TD([subQ5,makeQuery(id+"F25.opChamfer","BLEND_FACE",FACE,{"disambiguationData":[OSD([subQ0])]}),subQ4,makeQuery(id+"F29.opExtrude","SWEPT_FACE",FACE,{"disambiguationData":[OSD([sQuery(id+"F28.wireOp",EDGE,"E11.0.8.1")])]}),subQ7])],"derivedFrom":makeQuery(id+"F12.opExtrude","CAP_FACE",FACE,{"disambiguationData":[OSD([subQ3,subQ2,subQ1,subQ0])],"isStart":false})})]});}
            var Q14;
            {var subQ0=sQuery(id+"F11.wireOp",EDGE,"E1.top");var subQ1=makeQuery(id+"F25.opChamfer","BLEND_FACE",FACE,{"disambiguationData":[OSD([subQ0])]});var subQ2=sQuery(id+"F11.wireOp",EDGE,"E1.right");var subQ3=sQuery(id+"F11.wireOp",EDGE,"E1.left");var subQ4=sQuery(id+"F11.wireOp",EDGE,"E1.bottom");var subQ5=makeQuery(id+"F26.opChamfer","BLEND_FACE",FACE,{"disambiguationData":[OSD([subQ4,subQ0,subQ3,subQ2,sQuery(id+"F18.wireOp",EDGE,"E7")])]});var subQ6=sQuery(id+"F28.wireOp",EDGE,"E11.0.9.1");var subQ7=makeQuery(id+"F29.opExtrude","SWEPT_FACE",FACE,{"disambiguationData":[OSD([subQ6])]});Q14=makeQuery(id+"F30.opFillet","BLEND_EDGE",EDGE,{"blendedFrom":[makeQuery(id+"F29.boolean.opBoolean","COPY",EDGE,{"disambiguationData":[TD([subQ1])],"derivedFrom":makeQuery(id+"F29.opExtrude","CAP_EDGE",EDGE,{"disambiguationData":[OSD([subQ6])],"isStart":false})}),makeQuery(id+"F29.boolean.opBoolean","SPLIT",FACE,{"disambiguationData":[TD([subQ1,subQ5,subQ7,makeQuery(id+"F29.opExtrude","SWEPT_FACE",FACE,{"disambiguationData":[OSD([sQuery(id+"F28.wireOp",EDGE,"E11.0.10.0")])]})])],"derivedFrom":makeQuery(id+"F12.opExtrude","CAP_FACE",FACE,{"disambiguationData":[OSD([subQ4,subQ0,subQ3,subQ2])],"isStart":false})})],"blendedInto":[makeQuery(id+"F29.boolean.opBoolean","SPLIT",FACE,{"disambiguationData":[TD([subQ1,subQ5,subQ7,makeQuery(id+"F29.opExtrude","SWEPT_FACE",FACE,{"disambiguationData":[OSD([sQuery(id+"F28.wireOp",EDGE,"E11.0.10.0")])]})])],"derivedFrom":makeQuery(id+"F12.opExtrude","CAP_FACE",FACE,{"disambiguationData":[OSD([subQ4,subQ0,subQ3,subQ2])],"isStart":false})})]});}
            var Q15;
            {var subQ0=sQuery(id+"F11.wireOp",EDGE,"E1.top");var subQ1=makeQuery(id+"F25.opChamfer","BLEND_FACE",FACE,{"disambiguationData":[OSD([subQ0])]});var subQ2=sQuery(id+"F11.wireOp",EDGE,"E1.right");var subQ3=sQuery(id+"F11.wireOp",EDGE,"E1.left");var subQ4=sQuery(id+"F11.wireOp",EDGE,"E1.bottom");var subQ5=makeQuery(id+"F26.opChamfer","BLEND_FACE",FACE,{"disambiguationData":[OSD([subQ4,subQ0,subQ3,subQ2,sQuery(id+"F18.wireOp",EDGE,"E7")])]});var subQ6=sQuery(id+"F28.wireOp",EDGE,"E11.0.10.0");var subQ7=makeQuery(id+"F29.opExtrude","SWEPT_FACE",FACE,{"disambiguationData":[OSD([subQ6])]});Q15=makeQuery(id+"F30.opFillet","BLEND_EDGE",EDGE,{"blendedFrom":[makeQuery(id+"F29.boolean.opBoolean","COPY",EDGE,{"disambiguationData":[TD([subQ1])],"derivedFrom":makeQuery(id+"F29.opExtrude","CAP_EDGE",EDGE,{"disambiguationData":[OSD([subQ6])],"isStart":false})}),makeQuery(id+"F29.boolean.opBoolean","SPLIT",FACE,{"disambiguationData":[TD([subQ1,subQ5,makeQuery(id+"F29.opExtrude","SWEPT_FACE",FACE,{"disambiguationData":[OSD([sQuery(id+"F28.wireOp",EDGE,"E11.0.9.1")])]}),subQ7])],"derivedFrom":makeQuery(id+"F12.opExtrude","CAP_FACE",FACE,{"disambiguationData":[OSD([subQ4,subQ0,subQ3,subQ2])],"isStart":false})})],"blendedInto":[makeQuery(id+"F29.boolean.opBoolean","SPLIT",FACE,{"disambiguationData":[TD([subQ1,subQ5,makeQuery(id+"F29.opExtrude","SWEPT_FACE",FACE,{"disambiguationData":[OSD([sQuery(id+"F28.wireOp",EDGE,"E11.0.9.1")])]}),subQ7])],"derivedFrom":makeQuery(id+"F12.opExtrude","CAP_FACE",FACE,{"disambiguationData":[OSD([subQ4,subQ0,subQ3,subQ2])],"isStart":false})})]});}
            var Q16;
            {var subQ0=sQuery(id+"F11.wireOp",EDGE,"E1.top");var subQ1=makeQuery(id+"F25.opChamfer","BLEND_FACE",FACE,{"disambiguationData":[OSD([subQ0])]});var subQ2=sQuery(id+"F11.wireOp",EDGE,"E1.right");var subQ3=sQuery(id+"F11.wireOp",EDGE,"E1.left");var subQ4=sQuery(id+"F11.wireOp",EDGE,"E1.bottom");var subQ5=makeQuery(id+"F26.opChamfer","BLEND_FACE",FACE,{"disambiguationData":[OSD([subQ4,subQ0,subQ3,subQ2,sQuery(id+"F18.wireOp",EDGE,"E7")])]});var subQ6=sQuery(id+"F28.wireOp",EDGE,"E11.0.10.1");var subQ7=makeQuery(id+"F29.opExtrude","SWEPT_FACE",FACE,{"disambiguationData":[OSD([subQ6])]});Q16=makeQuery(id+"F30.opFillet","BLEND_EDGE",EDGE,{"blendedFrom":[makeQuery(id+"F29.boolean.opBoolean","COPY",EDGE,{"disambiguationData":[TD([subQ1])],"derivedFrom":makeQuery(id+"F29.opExtrude","CAP_EDGE",EDGE,{"disambiguationData":[OSD([subQ6])],"isStart":false})}),makeQuery(id+"F29.boolean.opBoolean","SPLIT",FACE,{"disambiguationData":[TD([subQ1,subQ5,subQ7,makeQuery(id+"F29.opExtrude","SWEPT_FACE",FACE,{"disambiguationData":[OSD([sQuery(id+"F28.wireOp",EDGE,"E11.0.11.0")])]})])],"derivedFrom":makeQuery(id+"F12.opExtrude","CAP_FACE",FACE,{"disambiguationData":[OSD([subQ4,subQ0,subQ3,subQ2])],"isStart":false})})],"blendedInto":[makeQuery(id+"F29.boolean.opBoolean","SPLIT",FACE,{"disambiguationData":[TD([subQ1,subQ5,subQ7,makeQuery(id+"F29.opExtrude","SWEPT_FACE",FACE,{"disambiguationData":[OSD([sQuery(id+"F28.wireOp",EDGE,"E11.0.11.0")])]})])],"derivedFrom":makeQuery(id+"F12.opExtrude","CAP_FACE",FACE,{"disambiguationData":[OSD([subQ4,subQ0,subQ3,subQ2])],"isStart":false})})]});}
            var Q17;
            {var subQ0=sQuery(id+"F11.wireOp",EDGE,"E1.top");var subQ1=makeQuery(id+"F25.opChamfer","BLEND_FACE",FACE,{"disambiguationData":[OSD([subQ0])]});var subQ2=sQuery(id+"F11.wireOp",EDGE,"E1.right");var subQ3=sQuery(id+"F11.wireOp",EDGE,"E1.left");var subQ4=sQuery(id+"F11.wireOp",EDGE,"E1.bottom");var subQ5=makeQuery(id+"F26.opChamfer","BLEND_FACE",FACE,{"disambiguationData":[OSD([subQ4,subQ0,subQ3,subQ2,sQuery(id+"F18.wireOp",EDGE,"E7")])]});var subQ6=sQuery(id+"F28.wireOp",EDGE,"E11.0.11.0");var subQ7=makeQuery(id+"F29.opExtrude","SWEPT_FACE",FACE,{"disambiguationData":[OSD([subQ6])]});Q17=makeQuery(id+"F30.opFillet","BLEND_EDGE",EDGE,{"blendedFrom":[makeQuery(id+"F29.boolean.opBoolean","COPY",EDGE,{"disambiguationData":[TD([subQ1])],"derivedFrom":makeQuery(id+"F29.opExtrude","CAP_EDGE",EDGE,{"disambiguationData":[OSD([subQ6])],"isStart":false})}),makeQuery(id+"F29.boolean.opBoolean","SPLIT",FACE,{"disambiguationData":[TD([subQ1,subQ5,makeQuery(id+"F29.opExtrude","SWEPT_FACE",FACE,{"disambiguationData":[OSD([sQuery(id+"F28.wireOp",EDGE,"E11.0.10.1")])]}),subQ7])],"derivedFrom":makeQuery(id+"F12.opExtrude","CAP_FACE",FACE,{"disambiguationData":[OSD([subQ4,subQ0,subQ3,subQ2])],"isStart":false})})],"blendedInto":[makeQuery(id+"F29.boolean.opBoolean","SPLIT",FACE,{"disambiguationData":[TD([subQ1,subQ5,makeQuery(id+"F29.opExtrude","SWEPT_FACE",FACE,{"disambiguationData":[OSD([sQuery(id+"F28.wireOp",EDGE,"E11.0.10.1")])]}),subQ7])],"derivedFrom":makeQuery(id+"F12.opExtrude","CAP_FACE",FACE,{"disambiguationData":[OSD([subQ4,subQ0,subQ3,subQ2])],"isStart":false})})]});}
            var Q18;
            {var subQ0=sQuery(id+"F28.wireOp",EDGE,"E11.0.11.1");var subQ1=makeQuery(id+"F29.opExtrude","SWEPT_FACE",FACE,{"disambiguationData":[OSD([subQ0])]});var subQ2=sQuery(id+"F11.wireOp",EDGE,"E1.left");var subQ3=sQuery(id+"F11.wireOp",EDGE,"E1.right");var subQ4=sQuery(id+"F11.wireOp",EDGE,"E1.top");var subQ5=sQuery(id+"F11.wireOp",EDGE,"E1.bottom");var subQ6=makeQuery(id+"F26.opChamfer","BLEND_FACE",FACE,{"disambiguationData":[OSD([subQ5,subQ4,subQ2,subQ3,sQuery(id+"F18.wireOp",EDGE,"E7")])]});var subQ7=makeQuery(id+"F25.opChamfer","BLEND_FACE",FACE,{"disambiguationData":[OSD([subQ4])]});Q18=makeQuery(id+"F30.opFillet","BLEND_EDGE",EDGE,{"blendedFrom":[makeQuery(id+"F29.boolean.opBoolean","COPY",EDGE,{"disambiguationData":[TD([subQ7])],"derivedFrom":makeQuery(id+"F29.opExtrude","CAP_EDGE",EDGE,{"disambiguationData":[OSD([subQ0])],"isStart":false})}),makeQuery(id+"F29.boolean.opBoolean","SPLIT",FACE,{"disambiguationData":[TD([subQ7,makeQuery(id+"F25.opChamfer","BLEND_FACE",FACE,{"disambiguationData":[OSD([subQ2])]}),subQ6,subQ1,makeQuery(id+"F29.opExtrude","SWEPT_FACE",FACE,{"disambiguationData":[OSD([sQuery(id+"F28.wireOp",EDGE,"E11.0.12.0")])]})])],"derivedFrom":makeQuery(id+"F12.opExtrude","CAP_FACE",FACE,{"disambiguationData":[OSD([subQ5,subQ4,subQ2,subQ3])],"isStart":false})})],"blendedInto":[makeQuery(id+"F29.boolean.opBoolean","SPLIT",FACE,{"disambiguationData":[TD([subQ7,makeQuery(id+"F25.opChamfer","BLEND_FACE",FACE,{"disambiguationData":[OSD([subQ2])]}),subQ6,subQ1,makeQuery(id+"F29.opExtrude","SWEPT_FACE",FACE,{"disambiguationData":[OSD([sQuery(id+"F28.wireOp",EDGE,"E11.0.12.0")])]})])],"derivedFrom":makeQuery(id+"F12.opExtrude","CAP_FACE",FACE,{"disambiguationData":[OSD([subQ5,subQ4,subQ2,subQ3])],"isStart":false})})]});}
            var Q19;
            {var subQ0=sQuery(id+"F11.wireOp",EDGE,"E1.left");var subQ1=sQuery(id+"F11.wireOp",EDGE,"E1.right");var subQ2=sQuery(id+"F11.wireOp",EDGE,"E1.top");var subQ3=sQuery(id+"F11.wireOp",EDGE,"E1.bottom");var subQ4=sQuery(id+"F28.wireOp",EDGE,"E11.0.12.0");Q19=makeQuery(id+"F30.opFillet","BLEND_EDGE",EDGE,{"blendedFrom":[makeQuery(id+"F29.boolean.opBoolean","COPY",EDGE,{"derivedFrom":makeQuery(id+"F29.opExtrude","CAP_EDGE",EDGE,{"disambiguationData":[OSD([subQ4])],"isStart":false})}),makeQuery(id+"F29.boolean.opBoolean","SPLIT",FACE,{"disambiguationData":[TD([makeQuery(id+"F25.opChamfer","BLEND_FACE",FACE,{"disambiguationData":[OSD([subQ2])]}),makeQuery(id+"F25.opChamfer","BLEND_FACE",FACE,{"disambiguationData":[OSD([subQ0])]}),makeQuery(id+"F26.opChamfer","BLEND_FACE",FACE,{"disambiguationData":[OSD([subQ3,subQ2,subQ0,subQ1,sQuery(id+"F18.wireOp",EDGE,"E7")])]}),makeQuery(id+"F29.opExtrude","SWEPT_FACE",FACE,{"disambiguationData":[OSD([sQuery(id+"F28.wireOp",EDGE,"E11.0.11.1")])]}),makeQuery(id+"F29.opExtrude","SWEPT_FACE",FACE,{"disambiguationData":[OSD([subQ4])]})])],"derivedFrom":makeQuery(id+"F12.opExtrude","CAP_FACE",FACE,{"disambiguationData":[OSD([subQ3,subQ2,subQ0,subQ1])],"isStart":false})})],"blendedInto":[makeQuery(id+"F29.boolean.opBoolean","SPLIT",FACE,{"disambiguationData":[TD([makeQuery(id+"F25.opChamfer","BLEND_FACE",FACE,{"disambiguationData":[OSD([subQ2])]}),makeQuery(id+"F25.opChamfer","BLEND_FACE",FACE,{"disambiguationData":[OSD([subQ0])]}),makeQuery(id+"F26.opChamfer","BLEND_FACE",FACE,{"disambiguationData":[OSD([subQ3,subQ2,subQ0,subQ1,sQuery(id+"F18.wireOp",EDGE,"E7")])]}),makeQuery(id+"F29.opExtrude","SWEPT_FACE",FACE,{"disambiguationData":[OSD([sQuery(id+"F28.wireOp",EDGE,"E11.0.11.1")])]}),makeQuery(id+"F29.opExtrude","SWEPT_FACE",FACE,{"disambiguationData":[OSD([subQ4])]})])],"derivedFrom":makeQuery(id+"F12.opExtrude","CAP_FACE",FACE,{"disambiguationData":[OSD([subQ3,subQ2,subQ0,subQ1])],"isStart":false})})]});}
            var Q20;
            {var subQ0=sQuery(id+"F11.wireOp",EDGE,"E1.top");var subQ1=sQuery(id+"F11.wireOp",EDGE,"E1.left");var subQ2=sQuery(id+"F28.wireOp",EDGE,"E11.0.12.1");Q20=makeQuery(id+"F30.opFillet","BLEND_EDGE",EDGE,{"blendedFrom":[makeQuery(id+"F29.boolean.opBoolean","COPY",EDGE,{"derivedFrom":makeQuery(id+"F29.opExtrude","CAP_EDGE",EDGE,{"disambiguationData":[OSD([subQ2])],"isStart":false})}),makeQuery(id+"F29.boolean.opBoolean","SPLIT",FACE,{"disambiguationData":[TD([makeQuery(id+"F25.opChamfer","BLEND_FACE",FACE,{"disambiguationData":[OSD([subQ0])]}),makeQuery(id+"F25.opChamfer","BLEND_FACE",FACE,{"disambiguationData":[OSD([subQ1])]}),makeQuery(id+"F29.opExtrude","SWEPT_FACE",FACE,{"disambiguationData":[OSD([subQ2])]})])],"derivedFrom":makeQuery(id+"F12.opExtrude","CAP_FACE",FACE,{"disambiguationData":[OSD([sQuery(id+"F11.wireOp",EDGE,"E1.bottom"),subQ0,subQ1,sQuery(id+"F11.wireOp",EDGE,"E1.right")])],"isStart":false})})],"blendedInto":[makeQuery(id+"F29.boolean.opBoolean","SPLIT",FACE,{"disambiguationData":[TD([makeQuery(id+"F25.opChamfer","BLEND_FACE",FACE,{"disambiguationData":[OSD([subQ0])]}),makeQuery(id+"F25.opChamfer","BLEND_FACE",FACE,{"disambiguationData":[OSD([subQ1])]}),makeQuery(id+"F29.opExtrude","SWEPT_FACE",FACE,{"disambiguationData":[OSD([subQ2])]})])],"derivedFrom":makeQuery(id+"F12.opExtrude","CAP_FACE",FACE,{"disambiguationData":[OSD([sQuery(id+"F11.wireOp",EDGE,"E1.bottom"),subQ0,subQ1,sQuery(id+"F11.wireOp",EDGE,"E1.right")])],"isStart":false})})]});}
            var Q21;
            {var subQ0=sQuery(id+"F11.wireOp",EDGE,"E1.left");var subQ1=makeQuery(id+"F25.opChamfer","BLEND_FACE",FACE,{"disambiguationData":[OSD([subQ0])]});var subQ2=sQuery(id+"F11.wireOp",EDGE,"E1.right");var subQ3=sQuery(id+"F11.wireOp",EDGE,"E1.top");var subQ4=sQuery(id+"F11.wireOp",EDGE,"E1.bottom");var subQ5=makeQuery(id+"F26.opChamfer","BLEND_FACE",FACE,{"disambiguationData":[OSD([subQ4,subQ3,subQ0,subQ2,sQuery(id+"F18.wireOp",EDGE,"E7")])]});var subQ6=sQuery(id+"F28.wireOp",EDGE,"E11.0.11.0");var subQ7=makeQuery(id+"F29.opExtrude","SWEPT_FACE",FACE,{"disambiguationData":[OSD([subQ6])]});Q21=makeQuery(id+"F30.opFillet","BLEND_EDGE",EDGE,{"blendedFrom":[makeQuery(id+"F29.boolean.opBoolean","COPY",EDGE,{"disambiguationData":[TD([subQ1])],"derivedFrom":makeQuery(id+"F29.opExtrude","CAP_EDGE",EDGE,{"disambiguationData":[OSD([subQ6])],"isStart":false})}),makeQuery(id+"F29.boolean.opBoolean","SPLIT",FACE,{"disambiguationData":[TD([subQ1,subQ5,makeQuery(id+"F29.opExtrude","SWEPT_FACE",FACE,{"disambiguationData":[OSD([sQuery(id+"F28.wireOp",EDGE,"E11.0.10.1")])]}),subQ7])],"derivedFrom":makeQuery(id+"F12.opExtrude","CAP_FACE",FACE,{"disambiguationData":[OSD([subQ4,subQ3,subQ0,subQ2])],"isStart":false})})],"blendedInto":[makeQuery(id+"F29.boolean.opBoolean","SPLIT",FACE,{"disambiguationData":[TD([subQ1,subQ5,makeQuery(id+"F29.opExtrude","SWEPT_FACE",FACE,{"disambiguationData":[OSD([sQuery(id+"F28.wireOp",EDGE,"E11.0.10.1")])]}),subQ7])],"derivedFrom":makeQuery(id+"F12.opExtrude","CAP_FACE",FACE,{"disambiguationData":[OSD([subQ4,subQ3,subQ0,subQ2])],"isStart":false})})]});}
            var Q22;
            {var subQ0=sQuery(id+"F28.wireOp",EDGE,"E11.0.11.1");var subQ1=makeQuery(id+"F29.opExtrude","SWEPT_FACE",FACE,{"disambiguationData":[OSD([subQ0])]});var subQ2=sQuery(id+"F11.wireOp",EDGE,"E1.left");var subQ3=makeQuery(id+"F25.opChamfer","BLEND_FACE",FACE,{"disambiguationData":[OSD([subQ2])]});var subQ4=sQuery(id+"F11.wireOp",EDGE,"E1.right");var subQ5=sQuery(id+"F11.wireOp",EDGE,"E1.top");var subQ6=sQuery(id+"F11.wireOp",EDGE,"E1.bottom");var subQ7=makeQuery(id+"F26.opChamfer","BLEND_FACE",FACE,{"disambiguationData":[OSD([subQ6,subQ5,subQ2,subQ4,sQuery(id+"F18.wireOp",EDGE,"E7")])]});Q22=makeQuery(id+"F30.opFillet","BLEND_EDGE",EDGE,{"blendedFrom":[makeQuery(id+"F29.boolean.opBoolean","COPY",EDGE,{"disambiguationData":[TD([subQ3])],"derivedFrom":makeQuery(id+"F29.opExtrude","CAP_EDGE",EDGE,{"disambiguationData":[OSD([subQ0])],"isStart":false})}),makeQuery(id+"F29.boolean.opBoolean","SPLIT",FACE,{"disambiguationData":[TD([makeQuery(id+"F25.opChamfer","BLEND_FACE",FACE,{"disambiguationData":[OSD([subQ5])]}),subQ3,subQ7,subQ1,makeQuery(id+"F29.opExtrude","SWEPT_FACE",FACE,{"disambiguationData":[OSD([sQuery(id+"F28.wireOp",EDGE,"E11.0.12.0")])]})])],"derivedFrom":makeQuery(id+"F12.opExtrude","CAP_FACE",FACE,{"disambiguationData":[OSD([subQ6,subQ5,subQ2,subQ4])],"isStart":false})})],"blendedInto":[makeQuery(id+"F29.boolean.opBoolean","SPLIT",FACE,{"disambiguationData":[TD([makeQuery(id+"F25.opChamfer","BLEND_FACE",FACE,{"disambiguationData":[OSD([subQ5])]}),subQ3,subQ7,subQ1,makeQuery(id+"F29.opExtrude","SWEPT_FACE",FACE,{"disambiguationData":[OSD([sQuery(id+"F28.wireOp",EDGE,"E11.0.12.0")])]})])],"derivedFrom":makeQuery(id+"F12.opExtrude","CAP_FACE",FACE,{"disambiguationData":[OSD([subQ6,subQ5,subQ2,subQ4])],"isStart":false})})]});}
            var Q23;
            {var subQ0=sQuery(id+"F11.wireOp",EDGE,"E1.left");var subQ1=makeQuery(id+"F25.opChamfer","BLEND_FACE",FACE,{"disambiguationData":[OSD([subQ0])]});var subQ2=sQuery(id+"F11.wireOp",EDGE,"E1.right");var subQ3=sQuery(id+"F11.wireOp",EDGE,"E1.top");var subQ4=sQuery(id+"F11.wireOp",EDGE,"E1.bottom");var subQ5=makeQuery(id+"F26.opChamfer","BLEND_FACE",FACE,{"disambiguationData":[OSD([subQ4,subQ3,subQ0,subQ2,sQuery(id+"F18.wireOp",EDGE,"E7")])]});var subQ6=sQuery(id+"F28.wireOp",EDGE,"E11.0.10.1");var subQ7=makeQuery(id+"F29.opExtrude","SWEPT_FACE",FACE,{"disambiguationData":[OSD([subQ6])]});Q23=makeQuery(id+"F30.opFillet","BLEND_EDGE",EDGE,{"blendedFrom":[makeQuery(id+"F29.boolean.opBoolean","COPY",EDGE,{"disambiguationData":[TD([subQ1])],"derivedFrom":makeQuery(id+"F29.opExtrude","CAP_EDGE",EDGE,{"disambiguationData":[OSD([subQ6])],"isStart":false})}),makeQuery(id+"F29.boolean.opBoolean","SPLIT",FACE,{"disambiguationData":[TD([subQ1,subQ5,subQ7,makeQuery(id+"F29.opExtrude","SWEPT_FACE",FACE,{"disambiguationData":[OSD([sQuery(id+"F28.wireOp",EDGE,"E11.0.11.0")])]})])],"derivedFrom":makeQuery(id+"F12.opExtrude","CAP_FACE",FACE,{"disambiguationData":[OSD([subQ4,subQ3,subQ0,subQ2])],"isStart":false})})],"blendedInto":[makeQuery(id+"F29.boolean.opBoolean","SPLIT",FACE,{"disambiguationData":[TD([subQ1,subQ5,subQ7,makeQuery(id+"F29.opExtrude","SWEPT_FACE",FACE,{"disambiguationData":[OSD([sQuery(id+"F28.wireOp",EDGE,"E11.0.11.0")])]})])],"derivedFrom":makeQuery(id+"F12.opExtrude","CAP_FACE",FACE,{"disambiguationData":[OSD([subQ4,subQ3,subQ0,subQ2])],"isStart":false})})]});}
            var Q24;
            {var subQ0=sQuery(id+"F11.wireOp",EDGE,"E1.left");var subQ1=makeQuery(id+"F25.opChamfer","BLEND_FACE",FACE,{"disambiguationData":[OSD([subQ0])]});var subQ2=sQuery(id+"F11.wireOp",EDGE,"E1.right");var subQ3=sQuery(id+"F11.wireOp",EDGE,"E1.top");var subQ4=sQuery(id+"F11.wireOp",EDGE,"E1.bottom");var subQ5=makeQuery(id+"F26.opChamfer","BLEND_FACE",FACE,{"disambiguationData":[OSD([subQ4,subQ3,subQ0,subQ2,sQuery(id+"F18.wireOp",EDGE,"E7")])]});var subQ6=sQuery(id+"F28.wireOp",EDGE,"E11.0.10.0");var subQ7=makeQuery(id+"F29.opExtrude","SWEPT_FACE",FACE,{"disambiguationData":[OSD([subQ6])]});Q24=makeQuery(id+"F30.opFillet","BLEND_EDGE",EDGE,{"blendedFrom":[makeQuery(id+"F29.boolean.opBoolean","COPY",EDGE,{"disambiguationData":[TD([subQ1])],"derivedFrom":makeQuery(id+"F29.opExtrude","CAP_EDGE",EDGE,{"disambiguationData":[OSD([subQ6])],"isStart":false})}),makeQuery(id+"F29.boolean.opBoolean","SPLIT",FACE,{"disambiguationData":[TD([subQ1,subQ5,makeQuery(id+"F29.opExtrude","SWEPT_FACE",FACE,{"disambiguationData":[OSD([sQuery(id+"F28.wireOp",EDGE,"E11.0.9.1")])]}),subQ7])],"derivedFrom":makeQuery(id+"F12.opExtrude","CAP_FACE",FACE,{"disambiguationData":[OSD([subQ4,subQ3,subQ0,subQ2])],"isStart":false})})],"blendedInto":[makeQuery(id+"F29.boolean.opBoolean","SPLIT",FACE,{"disambiguationData":[TD([subQ1,subQ5,makeQuery(id+"F29.opExtrude","SWEPT_FACE",FACE,{"disambiguationData":[OSD([sQuery(id+"F28.wireOp",EDGE,"E11.0.9.1")])]}),subQ7])],"derivedFrom":makeQuery(id+"F12.opExtrude","CAP_FACE",FACE,{"disambiguationData":[OSD([subQ4,subQ3,subQ0,subQ2])],"isStart":false})})]});}
            var Q25;
            {var subQ0=sQuery(id+"F11.wireOp",EDGE,"E1.left");var subQ1=makeQuery(id+"F25.opChamfer","BLEND_FACE",FACE,{"disambiguationData":[OSD([subQ0])]});var subQ2=sQuery(id+"F28.wireOp",EDGE,"E11.0.9.0");var subQ3=makeQuery(id+"F29.opExtrude","SWEPT_FACE",FACE,{"disambiguationData":[OSD([subQ2])]});var subQ4=sQuery(id+"F11.wireOp",EDGE,"E1.right");var subQ5=sQuery(id+"F11.wireOp",EDGE,"E1.top");var subQ6=sQuery(id+"F11.wireOp",EDGE,"E1.bottom");var subQ7=makeQuery(id+"F26.opChamfer","BLEND_FACE",FACE,{"disambiguationData":[OSD([subQ6,subQ5,subQ0,subQ4,sQuery(id+"F18.wireOp",EDGE,"E7")])]});Q25=makeQuery(id+"F30.opFillet","BLEND_EDGE",EDGE,{"blendedFrom":[makeQuery(id+"F29.boolean.opBoolean","COPY",EDGE,{"disambiguationData":[TD([subQ1])],"derivedFrom":makeQuery(id+"F29.opExtrude","CAP_EDGE",EDGE,{"disambiguationData":[OSD([subQ2])],"isStart":false})}),makeQuery(id+"F29.boolean.opBoolean","SPLIT",FACE,{"disambiguationData":[TD([subQ1,subQ7,makeQuery(id+"F29.opExtrude","SWEPT_FACE",FACE,{"disambiguationData":[OSD([sQuery(id+"F28.wireOp",EDGE,"E11.0.8.1")])]}),subQ3])],"derivedFrom":makeQuery(id+"F12.opExtrude","CAP_FACE",FACE,{"disambiguationData":[OSD([subQ6,subQ5,subQ0,subQ4])],"isStart":false})})],"blendedInto":[makeQuery(id+"F29.boolean.opBoolean","SPLIT",FACE,{"disambiguationData":[TD([subQ1,subQ7,makeQuery(id+"F29.opExtrude","SWEPT_FACE",FACE,{"disambiguationData":[OSD([sQuery(id+"F28.wireOp",EDGE,"E11.0.8.1")])]}),subQ3])],"derivedFrom":makeQuery(id+"F12.opExtrude","CAP_FACE",FACE,{"disambiguationData":[OSD([subQ6,subQ5,subQ0,subQ4])],"isStart":false})})]});}
            var Q26;
            {var subQ0=sQuery(id+"F11.wireOp",EDGE,"E1.left");var subQ1=makeQuery(id+"F25.opChamfer","BLEND_FACE",FACE,{"disambiguationData":[OSD([subQ0])]});var subQ2=sQuery(id+"F11.wireOp",EDGE,"E1.right");var subQ3=sQuery(id+"F11.wireOp",EDGE,"E1.top");var subQ4=sQuery(id+"F11.wireOp",EDGE,"E1.bottom");var subQ5=makeQuery(id+"F26.opChamfer","BLEND_FACE",FACE,{"disambiguationData":[OSD([subQ4,subQ3,subQ0,subQ2,sQuery(id+"F18.wireOp",EDGE,"E7")])]});var subQ6=sQuery(id+"F28.wireOp",EDGE,"E11.0.9.1");var subQ7=makeQuery(id+"F29.opExtrude","SWEPT_FACE",FACE,{"disambiguationData":[OSD([subQ6])]});Q26=makeQuery(id+"F30.opFillet","BLEND_EDGE",EDGE,{"blendedFrom":[makeQuery(id+"F29.boolean.opBoolean","COPY",EDGE,{"disambiguationData":[TD([subQ1])],"derivedFrom":makeQuery(id+"F29.opExtrude","CAP_EDGE",EDGE,{"disambiguationData":[OSD([subQ6])],"isStart":false})}),makeQuery(id+"F29.boolean.opBoolean","SPLIT",FACE,{"disambiguationData":[TD([subQ1,subQ5,subQ7,makeQuery(id+"F29.opExtrude","SWEPT_FACE",FACE,{"disambiguationData":[OSD([sQuery(id+"F28.wireOp",EDGE,"E11.0.10.0")])]})])],"derivedFrom":makeQuery(id+"F12.opExtrude","CAP_FACE",FACE,{"disambiguationData":[OSD([subQ4,subQ3,subQ0,subQ2])],"isStart":false})})],"blendedInto":[makeQuery(id+"F29.boolean.opBoolean","SPLIT",FACE,{"disambiguationData":[TD([subQ1,subQ5,subQ7,makeQuery(id+"F29.opExtrude","SWEPT_FACE",FACE,{"disambiguationData":[OSD([sQuery(id+"F28.wireOp",EDGE,"E11.0.10.0")])]})])],"derivedFrom":makeQuery(id+"F12.opExtrude","CAP_FACE",FACE,{"disambiguationData":[OSD([subQ4,subQ3,subQ0,subQ2])],"isStart":false})})]});}
            var Q27;
            {var subQ0=sQuery(id+"F11.wireOp",EDGE,"E1.left");var subQ1=makeQuery(id+"F25.opChamfer","BLEND_FACE",FACE,{"disambiguationData":[OSD([subQ0])]});var subQ2=sQuery(id+"F11.wireOp",EDGE,"E1.right");var subQ3=sQuery(id+"F11.wireOp",EDGE,"E1.top");var subQ4=sQuery(id+"F11.wireOp",EDGE,"E1.bottom");var subQ5=makeQuery(id+"F26.opChamfer","BLEND_FACE",FACE,{"disambiguationData":[OSD([subQ4,subQ3,subQ0,subQ2,sQuery(id+"F18.wireOp",EDGE,"E7")])]});var subQ6=sQuery(id+"F28.wireOp",EDGE,"E11.0.8.0");var subQ7=makeQuery(id+"F29.opExtrude","SWEPT_FACE",FACE,{"disambiguationData":[OSD([subQ6])]});Q27=makeQuery(id+"F30.opFillet","BLEND_EDGE",EDGE,{"blendedFrom":[makeQuery(id+"F29.boolean.opBoolean","COPY",EDGE,{"disambiguationData":[TD([subQ1])],"derivedFrom":makeQuery(id+"F29.opExtrude","CAP_EDGE",EDGE,{"disambiguationData":[OSD([subQ6])],"isStart":false})}),makeQuery(id+"F29.boolean.opBoolean","SPLIT",FACE,{"disambiguationData":[TD([subQ1,subQ5,makeQuery(id+"F29.opExtrude","SWEPT_FACE",FACE,{"disambiguationData":[OSD([sQuery(id+"F28.wireOp",EDGE,"E11.0.7.1")])]}),subQ7])],"derivedFrom":makeQuery(id+"F12.opExtrude","CAP_FACE",FACE,{"disambiguationData":[OSD([subQ4,subQ3,subQ0,subQ2])],"isStart":false})})],"blendedInto":[makeQuery(id+"F29.boolean.opBoolean","SPLIT",FACE,{"disambiguationData":[TD([subQ1,subQ5,makeQuery(id+"F29.opExtrude","SWEPT_FACE",FACE,{"disambiguationData":[OSD([sQuery(id+"F28.wireOp",EDGE,"E11.0.7.1")])]}),subQ7])],"derivedFrom":makeQuery(id+"F12.opExtrude","CAP_FACE",FACE,{"disambiguationData":[OSD([subQ4,subQ3,subQ0,subQ2])],"isStart":false})})]});}
            var Q28;
            {var subQ0=sQuery(id+"F11.wireOp",EDGE,"E1.left");var subQ1=makeQuery(id+"F25.opChamfer","BLEND_FACE",FACE,{"disambiguationData":[OSD([subQ0])]});var subQ2=sQuery(id+"F11.wireOp",EDGE,"E1.right");var subQ3=sQuery(id+"F11.wireOp",EDGE,"E1.top");var subQ4=sQuery(id+"F11.wireOp",EDGE,"E1.bottom");var subQ5=makeQuery(id+"F26.opChamfer","BLEND_FACE",FACE,{"disambiguationData":[OSD([subQ4,subQ3,subQ0,subQ2,sQuery(id+"F18.wireOp",EDGE,"E7")])]});var subQ6=sQuery(id+"F28.wireOp",EDGE,"E11.0.8.1");var subQ7=makeQuery(id+"F29.opExtrude","SWEPT_FACE",FACE,{"disambiguationData":[OSD([subQ6])]});Q28=makeQuery(id+"F30.opFillet","BLEND_EDGE",EDGE,{"blendedFrom":[makeQuery(id+"F29.boolean.opBoolean","COPY",EDGE,{"disambiguationData":[TD([subQ1])],"derivedFrom":makeQuery(id+"F29.opExtrude","CAP_EDGE",EDGE,{"disambiguationData":[OSD([subQ6])],"isStart":false})}),makeQuery(id+"F29.boolean.opBoolean","SPLIT",FACE,{"disambiguationData":[TD([subQ1,subQ5,subQ7,makeQuery(id+"F29.opExtrude","SWEPT_FACE",FACE,{"disambiguationData":[OSD([sQuery(id+"F28.wireOp",EDGE,"E11.0.9.0")])]})])],"derivedFrom":makeQuery(id+"F12.opExtrude","CAP_FACE",FACE,{"disambiguationData":[OSD([subQ4,subQ3,subQ0,subQ2])],"isStart":false})})],"blendedInto":[makeQuery(id+"F29.boolean.opBoolean","SPLIT",FACE,{"disambiguationData":[TD([subQ1,subQ5,subQ7,makeQuery(id+"F29.opExtrude","SWEPT_FACE",FACE,{"disambiguationData":[OSD([sQuery(id+"F28.wireOp",EDGE,"E11.0.9.0")])]})])],"derivedFrom":makeQuery(id+"F12.opExtrude","CAP_FACE",FACE,{"disambiguationData":[OSD([subQ4,subQ3,subQ0,subQ2])],"isStart":false})})]});}
            var Q29;
            {var subQ0=sQuery(id+"F11.wireOp",EDGE,"E1.right");var subQ1=sQuery(id+"F11.wireOp",EDGE,"E1.left");var subQ2=sQuery(id+"F11.wireOp",EDGE,"E1.top");var subQ3=sQuery(id+"F11.wireOp",EDGE,"E1.bottom");var subQ4=makeQuery(id+"F26.opChamfer","BLEND_FACE",FACE,{"disambiguationData":[OSD([subQ3,subQ2,subQ1,subQ0,sQuery(id+"F18.wireOp",EDGE,"E7")])]});var subQ5=sQuery(id+"F28.wireOp",EDGE,"E11.0.7.0");var subQ6=makeQuery(id+"F29.opExtrude","SWEPT_FACE",FACE,{"disambiguationData":[OSD([subQ5])]});var subQ7=makeQuery(id+"F25.opChamfer","BLEND_FACE",FACE,{"disambiguationData":[OSD([subQ1])]});Q29=makeQuery(id+"F30.opFillet","BLEND_EDGE",EDGE,{"blendedFrom":[makeQuery(id+"F29.boolean.opBoolean","COPY",EDGE,{"disambiguationData":[TD([subQ7])],"derivedFrom":makeQuery(id+"F29.opExtrude","CAP_EDGE",EDGE,{"disambiguationData":[OSD([subQ5])],"isStart":false})}),makeQuery(id+"F29.boolean.opBoolean","SPLIT",FACE,{"disambiguationData":[TD([subQ7,subQ4,makeQuery(id+"F27.opChamfer","BLEND_FACE",FACE,{"disambiguationData":[OSD([subQ3,subQ2,subQ1,subQ0,sQuery(id+"F22.wireOp",EDGE,"E9")])]}),makeQuery(id+"F29.opExtrude","SWEPT_FACE",FACE,{"disambiguationData":[OSD([sQuery(id+"F28.wireOp",EDGE,"E11.0.6.1")])]}),subQ6])],"derivedFrom":makeQuery(id+"F12.opExtrude","CAP_FACE",FACE,{"disambiguationData":[OSD([subQ3,subQ2,subQ1,subQ0])],"isStart":false})})],"blendedInto":[makeQuery(id+"F29.boolean.opBoolean","SPLIT",FACE,{"disambiguationData":[TD([subQ7,subQ4,makeQuery(id+"F27.opChamfer","BLEND_FACE",FACE,{"disambiguationData":[OSD([subQ3,subQ2,subQ1,subQ0,sQuery(id+"F22.wireOp",EDGE,"E9")])]}),makeQuery(id+"F29.opExtrude","SWEPT_FACE",FACE,{"disambiguationData":[OSD([sQuery(id+"F28.wireOp",EDGE,"E11.0.6.1")])]}),subQ6])],"derivedFrom":makeQuery(id+"F12.opExtrude","CAP_FACE",FACE,{"disambiguationData":[OSD([subQ3,subQ2,subQ1,subQ0])],"isStart":false})})]});}
            var Q30;
            {var subQ0=sQuery(id+"F11.wireOp",EDGE,"E1.left");var subQ1=makeQuery(id+"F25.opChamfer","BLEND_FACE",FACE,{"disambiguationData":[OSD([subQ0])]});var subQ2=sQuery(id+"F11.wireOp",EDGE,"E1.right");var subQ3=sQuery(id+"F11.wireOp",EDGE,"E1.top");var subQ4=sQuery(id+"F11.wireOp",EDGE,"E1.bottom");var subQ5=makeQuery(id+"F26.opChamfer","BLEND_FACE",FACE,{"disambiguationData":[OSD([subQ4,subQ3,subQ0,subQ2,sQuery(id+"F18.wireOp",EDGE,"E7")])]});var subQ6=sQuery(id+"F28.wireOp",EDGE,"E11.0.7.1");var subQ7=makeQuery(id+"F29.opExtrude","SWEPT_FACE",FACE,{"disambiguationData":[OSD([subQ6])]});Q30=makeQuery(id+"F30.opFillet","BLEND_EDGE",EDGE,{"blendedFrom":[makeQuery(id+"F29.boolean.opBoolean","COPY",EDGE,{"disambiguationData":[TD([subQ1])],"derivedFrom":makeQuery(id+"F29.opExtrude","CAP_EDGE",EDGE,{"disambiguationData":[OSD([subQ6])],"isStart":false})}),makeQuery(id+"F29.boolean.opBoolean","SPLIT",FACE,{"disambiguationData":[TD([subQ1,subQ5,subQ7,makeQuery(id+"F29.opExtrude","SWEPT_FACE",FACE,{"disambiguationData":[OSD([sQuery(id+"F28.wireOp",EDGE,"E11.0.8.0")])]})])],"derivedFrom":makeQuery(id+"F12.opExtrude","CAP_FACE",FACE,{"disambiguationData":[OSD([subQ4,subQ3,subQ0,subQ2])],"isStart":false})})],"blendedInto":[makeQuery(id+"F29.boolean.opBoolean","SPLIT",FACE,{"disambiguationData":[TD([subQ1,subQ5,subQ7,makeQuery(id+"F29.opExtrude","SWEPT_FACE",FACE,{"disambiguationData":[OSD([sQuery(id+"F28.wireOp",EDGE,"E11.0.8.0")])]})])],"derivedFrom":makeQuery(id+"F12.opExtrude","CAP_FACE",FACE,{"disambiguationData":[OSD([subQ4,subQ3,subQ0,subQ2])],"isStart":false})})]});}
            var Q31;
            {var subQ0=sQuery(id+"F11.wireOp",EDGE,"E1.right");var subQ1=sQuery(id+"F11.wireOp",EDGE,"E1.left");var subQ2=sQuery(id+"F11.wireOp",EDGE,"E1.top");var subQ3=sQuery(id+"F11.wireOp",EDGE,"E1.bottom");var subQ4=makeQuery(id+"F27.opChamfer","BLEND_FACE",FACE,{"disambiguationData":[OSD([subQ3,subQ2,subQ1,subQ0,sQuery(id+"F22.wireOp",EDGE,"E9")])]});var subQ5=makeQuery(id+"F26.opChamfer","BLEND_FACE",FACE,{"disambiguationData":[OSD([subQ3,subQ2,subQ1,subQ0,sQuery(id+"F18.wireOp",EDGE,"E7")])]});var subQ6=sQuery(id+"F28.wireOp",EDGE,"E11.0.6.0");var subQ7=makeQuery(id+"F29.opExtrude","SWEPT_FACE",FACE,{"disambiguationData":[OSD([subQ6])]});Q31=makeQuery(id+"F30.opFillet","BLEND_EDGE",EDGE,{"blendedFrom":[makeQuery(id+"F29.boolean.opBoolean","COPY",EDGE,{"disambiguationData":[TD([subQ5,subQ4,subQ7,makeQuery(id+"F29.opExtrude","CAP_FACE",FACE,{"disambiguationData":[OSD([subQ6,sQuery(id+"F28.wireOp",EDGE,"E11.0.6.1"),sQuery(id+"F28.wireOp",EDGE,"E11.0.6.2"),sQuery(id+"F28.wireOp",EDGE,"E11.0.6.3")])],"isStart":false})])],"derivedFrom":makeQuery(id+"F29.opExtrude","CAP_EDGE",EDGE,{"disambiguationData":[OSD([subQ6])],"isStart":false})}),makeQuery(id+"F29.boolean.opBoolean","SPLIT",FACE,{"disambiguationData":[TD([makeQuery(id+"F25.opChamfer","BLEND_FACE",FACE,{"disambiguationData":[OSD([subQ0])]}),subQ5,subQ4,makeQuery(id+"F29.opExtrude","SWEPT_FACE",FACE,{"disambiguationData":[OSD([sQuery(id+"F28.wireOp",EDGE,"E11.0.5.1")])]}),subQ7])],"derivedFrom":makeQuery(id+"F12.opExtrude","CAP_FACE",FACE,{"disambiguationData":[OSD([subQ3,subQ2,subQ1,subQ0])],"isStart":false})})],"blendedInto":[makeQuery(id+"F29.boolean.opBoolean","SPLIT",FACE,{"disambiguationData":[TD([makeQuery(id+"F25.opChamfer","BLEND_FACE",FACE,{"disambiguationData":[OSD([subQ0])]}),subQ5,subQ4,makeQuery(id+"F29.opExtrude","SWEPT_FACE",FACE,{"disambiguationData":[OSD([sQuery(id+"F28.wireOp",EDGE,"E11.0.5.1")])]}),subQ7])],"derivedFrom":makeQuery(id+"F12.opExtrude","CAP_FACE",FACE,{"disambiguationData":[OSD([subQ3,subQ2,subQ1,subQ0])],"isStart":false})})]});}
            var Q32;
            {var subQ0=sQuery(id+"F11.wireOp",EDGE,"E1.right");var subQ1=sQuery(id+"F11.wireOp",EDGE,"E1.left");var subQ2=sQuery(id+"F11.wireOp",EDGE,"E1.top");var subQ3=sQuery(id+"F11.wireOp",EDGE,"E1.bottom");var subQ4=makeQuery(id+"F26.opChamfer","BLEND_FACE",FACE,{"disambiguationData":[OSD([subQ3,subQ2,subQ1,subQ0,sQuery(id+"F18.wireOp",EDGE,"E7")])]});var subQ5=sQuery(id+"F28.wireOp",EDGE,"E11.0.6.1");var subQ6=makeQuery(id+"F29.opExtrude","SWEPT_FACE",FACE,{"disambiguationData":[OSD([subQ5])]});var subQ7=makeQuery(id+"F27.opChamfer","BLEND_FACE",FACE,{"disambiguationData":[OSD([subQ3,subQ2,subQ1,subQ0,sQuery(id+"F22.wireOp",EDGE,"E9")])]});Q32=makeQuery(id+"F30.opFillet","BLEND_EDGE",EDGE,{"blendedFrom":[makeQuery(id+"F29.boolean.opBoolean","COPY",EDGE,{"disambiguationData":[TD([subQ4,subQ7,makeQuery(id+"F29.opExtrude","CAP_FACE",FACE,{"disambiguationData":[OSD([sQuery(id+"F28.wireOp",EDGE,"E11.0.6.0"),subQ5,sQuery(id+"F28.wireOp",EDGE,"E11.0.6.2"),sQuery(id+"F28.wireOp",EDGE,"E11.0.6.3")])],"isStart":false}),subQ6])],"derivedFrom":makeQuery(id+"F29.opExtrude","CAP_EDGE",EDGE,{"disambiguationData":[OSD([subQ5])],"isStart":false})}),makeQuery(id+"F29.boolean.opBoolean","SPLIT",FACE,{"disambiguationData":[TD([makeQuery(id+"F25.opChamfer","BLEND_FACE",FACE,{"disambiguationData":[OSD([subQ1])]}),subQ4,subQ7,subQ6,makeQuery(id+"F29.opExtrude","SWEPT_FACE",FACE,{"disambiguationData":[OSD([sQuery(id+"F28.wireOp",EDGE,"E11.0.7.0")])]})])],"derivedFrom":makeQuery(id+"F12.opExtrude","CAP_FACE",FACE,{"disambiguationData":[OSD([subQ3,subQ2,subQ1,subQ0])],"isStart":false})})],"blendedInto":[makeQuery(id+"F29.boolean.opBoolean","SPLIT",FACE,{"disambiguationData":[TD([makeQuery(id+"F25.opChamfer","BLEND_FACE",FACE,{"disambiguationData":[OSD([subQ1])]}),subQ4,subQ7,subQ6,makeQuery(id+"F29.opExtrude","SWEPT_FACE",FACE,{"disambiguationData":[OSD([sQuery(id+"F28.wireOp",EDGE,"E11.0.7.0")])]})])],"derivedFrom":makeQuery(id+"F12.opExtrude","CAP_FACE",FACE,{"disambiguationData":[OSD([subQ3,subQ2,subQ1,subQ0])],"isStart":false})})]});}
            var Q33;
            {var subQ0=sQuery(id+"F11.wireOp",EDGE,"E1.right");var subQ1=sQuery(id+"F11.wireOp",EDGE,"E1.left");var subQ2=sQuery(id+"F11.wireOp",EDGE,"E1.top");var subQ3=sQuery(id+"F11.wireOp",EDGE,"E1.bottom");var subQ4=makeQuery(id+"F27.opChamfer","BLEND_FACE",FACE,{"disambiguationData":[OSD([subQ3,subQ2,subQ1,subQ0,sQuery(id+"F22.wireOp",EDGE,"E9")])]});var subQ5=makeQuery(id+"F25.opChamfer","BLEND_FACE",FACE,{"disambiguationData":[OSD([subQ1])]});var subQ6=sQuery(id+"F28.wireOp",EDGE,"E11.0.6.0");var subQ7=makeQuery(id+"F29.opExtrude","SWEPT_FACE",FACE,{"disambiguationData":[OSD([subQ6])]});Q33=makeQuery(id+"F30.opFillet","BLEND_EDGE",EDGE,{"blendedFrom":[makeQuery(id+"F29.boolean.opBoolean","COPY",EDGE,{"disambiguationData":[TD([subQ5,subQ4,subQ7,makeQuery(id+"F29.opExtrude","CAP_FACE",FACE,{"disambiguationData":[OSD([subQ6,sQuery(id+"F28.wireOp",EDGE,"E11.0.6.1"),sQuery(id+"F28.wireOp",EDGE,"E11.0.6.2"),sQuery(id+"F28.wireOp",EDGE,"E11.0.6.3")])],"isStart":false})])],"derivedFrom":makeQuery(id+"F29.opExtrude","CAP_EDGE",EDGE,{"disambiguationData":[OSD([subQ6])],"isStart":false})}),makeQuery(id+"F29.boolean.opBoolean","SPLIT",FACE,{"disambiguationData":[TD([makeQuery(id+"F25.opChamfer","BLEND_FACE",FACE,{"disambiguationData":[OSD([subQ3])]}),subQ5,subQ4,makeQuery(id+"F29.opExtrude","SWEPT_FACE",FACE,{"disambiguationData":[OSD([sQuery(id+"F28.wireOp",EDGE,"E11.0.5.1")])]}),subQ7])],"derivedFrom":makeQuery(id+"F12.opExtrude","CAP_FACE",FACE,{"disambiguationData":[OSD([subQ3,subQ2,subQ1,subQ0])],"isStart":false})})],"blendedInto":[makeQuery(id+"F29.boolean.opBoolean","SPLIT",FACE,{"disambiguationData":[TD([makeQuery(id+"F25.opChamfer","BLEND_FACE",FACE,{"disambiguationData":[OSD([subQ3])]}),subQ5,subQ4,makeQuery(id+"F29.opExtrude","SWEPT_FACE",FACE,{"disambiguationData":[OSD([sQuery(id+"F28.wireOp",EDGE,"E11.0.5.1")])]}),subQ7])],"derivedFrom":makeQuery(id+"F12.opExtrude","CAP_FACE",FACE,{"disambiguationData":[OSD([subQ3,subQ2,subQ1,subQ0])],"isStart":false})})]});}
            var Q34;
            {var subQ0=sQuery(id+"F11.wireOp",EDGE,"E1.right");var subQ1=sQuery(id+"F11.wireOp",EDGE,"E1.left");var subQ2=sQuery(id+"F11.wireOp",EDGE,"E1.top");var subQ3=sQuery(id+"F11.wireOp",EDGE,"E1.bottom");var subQ4=sQuery(id+"F28.wireOp",EDGE,"E11.0.6.1");var subQ5=makeQuery(id+"F29.opExtrude","SWEPT_FACE",FACE,{"disambiguationData":[OSD([subQ4])]});var subQ6=makeQuery(id+"F27.opChamfer","BLEND_FACE",FACE,{"disambiguationData":[OSD([subQ3,subQ2,subQ1,subQ0,sQuery(id+"F22.wireOp",EDGE,"E9")])]});var subQ7=makeQuery(id+"F25.opChamfer","BLEND_FACE",FACE,{"disambiguationData":[OSD([subQ1])]});Q34=makeQuery(id+"F30.opFillet","BLEND_EDGE",EDGE,{"blendedFrom":[makeQuery(id+"F29.boolean.opBoolean","COPY",EDGE,{"disambiguationData":[TD([subQ7,subQ6,makeQuery(id+"F29.opExtrude","CAP_FACE",FACE,{"disambiguationData":[OSD([sQuery(id+"F28.wireOp",EDGE,"E11.0.6.0"),subQ4,sQuery(id+"F28.wireOp",EDGE,"E11.0.6.2"),sQuery(id+"F28.wireOp",EDGE,"E11.0.6.3")])],"isStart":false}),subQ5])],"derivedFrom":makeQuery(id+"F29.opExtrude","CAP_EDGE",EDGE,{"disambiguationData":[OSD([subQ4])],"isStart":false})}),makeQuery(id+"F29.boolean.opBoolean","SPLIT",FACE,{"disambiguationData":[TD([subQ7,makeQuery(id+"F26.opChamfer","BLEND_FACE",FACE,{"disambiguationData":[OSD([subQ3,subQ2,subQ1,subQ0,sQuery(id+"F18.wireOp",EDGE,"E7")])]}),subQ6,subQ5,makeQuery(id+"F29.opExtrude","SWEPT_FACE",FACE,{"disambiguationData":[OSD([sQuery(id+"F28.wireOp",EDGE,"E11.0.7.0")])]})])],"derivedFrom":makeQuery(id+"F12.opExtrude","CAP_FACE",FACE,{"disambiguationData":[OSD([subQ3,subQ2,subQ1,subQ0])],"isStart":false})})],"blendedInto":[makeQuery(id+"F29.boolean.opBoolean","SPLIT",FACE,{"disambiguationData":[TD([subQ7,makeQuery(id+"F26.opChamfer","BLEND_FACE",FACE,{"disambiguationData":[OSD([subQ3,subQ2,subQ1,subQ0,sQuery(id+"F18.wireOp",EDGE,"E7")])]}),subQ6,subQ5,makeQuery(id+"F29.opExtrude","SWEPT_FACE",FACE,{"disambiguationData":[OSD([sQuery(id+"F28.wireOp",EDGE,"E11.0.7.0")])]})])],"derivedFrom":makeQuery(id+"F12.opExtrude","CAP_FACE",FACE,{"disambiguationData":[OSD([subQ3,subQ2,subQ1,subQ0])],"isStart":false})})]});}
            var Q35;
            {var subQ0=sQuery(id+"F11.wireOp",EDGE,"E1.bottom");var subQ1=makeQuery(id+"F25.opChamfer","BLEND_FACE",FACE,{"disambiguationData":[OSD([subQ0])]});var subQ2=sQuery(id+"F11.wireOp",EDGE,"E1.right");var subQ3=sQuery(id+"F11.wireOp",EDGE,"E1.left");var subQ4=sQuery(id+"F11.wireOp",EDGE,"E1.top");var subQ5=makeQuery(id+"F27.opChamfer","BLEND_FACE",FACE,{"disambiguationData":[OSD([subQ0,subQ4,subQ3,subQ2,sQuery(id+"F22.wireOp",EDGE,"E9")])]});var subQ6=sQuery(id+"F28.wireOp",EDGE,"E11.0.5.0");var subQ7=makeQuery(id+"F29.opExtrude","SWEPT_FACE",FACE,{"disambiguationData":[OSD([subQ6])]});Q35=makeQuery(id+"F30.opFillet","BLEND_EDGE",EDGE,{"blendedFrom":[makeQuery(id+"F29.boolean.opBoolean","COPY",EDGE,{"disambiguationData":[TD([subQ1])],"derivedFrom":makeQuery(id+"F29.opExtrude","CAP_EDGE",EDGE,{"disambiguationData":[OSD([subQ6])],"isStart":false})}),makeQuery(id+"F29.boolean.opBoolean","SPLIT",FACE,{"disambiguationData":[TD([subQ1,subQ5,makeQuery(id+"F29.opExtrude","SWEPT_FACE",FACE,{"disambiguationData":[OSD([sQuery(id+"F28.wireOp",EDGE,"E11.0.4.1")])]}),subQ7])],"derivedFrom":makeQuery(id+"F12.opExtrude","CAP_FACE",FACE,{"disambiguationData":[OSD([subQ0,subQ4,subQ3,subQ2])],"isStart":false})})],"blendedInto":[makeQuery(id+"F29.boolean.opBoolean","SPLIT",FACE,{"disambiguationData":[TD([subQ1,subQ5,makeQuery(id+"F29.opExtrude","SWEPT_FACE",FACE,{"disambiguationData":[OSD([sQuery(id+"F28.wireOp",EDGE,"E11.0.4.1")])]}),subQ7])],"derivedFrom":makeQuery(id+"F12.opExtrude","CAP_FACE",FACE,{"disambiguationData":[OSD([subQ0,subQ4,subQ3,subQ2])],"isStart":false})})]});}
            var Q36;
            {var subQ0=sQuery(id+"F28.wireOp",EDGE,"E11.0.5.1");var subQ1=makeQuery(id+"F29.opExtrude","SWEPT_FACE",FACE,{"disambiguationData":[OSD([subQ0])]});var subQ2=sQuery(id+"F11.wireOp",EDGE,"E1.right");var subQ3=sQuery(id+"F11.wireOp",EDGE,"E1.left");var subQ4=sQuery(id+"F11.wireOp",EDGE,"E1.top");var subQ5=sQuery(id+"F11.wireOp",EDGE,"E1.bottom");var subQ6=makeQuery(id+"F27.opChamfer","BLEND_FACE",FACE,{"disambiguationData":[OSD([subQ5,subQ4,subQ3,subQ2,sQuery(id+"F22.wireOp",EDGE,"E9")])]});var subQ7=makeQuery(id+"F25.opChamfer","BLEND_FACE",FACE,{"disambiguationData":[OSD([subQ5])]});Q36=makeQuery(id+"F30.opFillet","BLEND_EDGE",EDGE,{"blendedFrom":[makeQuery(id+"F29.boolean.opBoolean","COPY",EDGE,{"disambiguationData":[TD([subQ7])],"derivedFrom":makeQuery(id+"F29.opExtrude","CAP_EDGE",EDGE,{"disambiguationData":[OSD([subQ0])],"isStart":false})}),makeQuery(id+"F29.boolean.opBoolean","SPLIT",FACE,{"disambiguationData":[TD([subQ7,makeQuery(id+"F25.opChamfer","BLEND_FACE",FACE,{"disambiguationData":[OSD([subQ3])]}),subQ6,subQ1,makeQuery(id+"F29.opExtrude","SWEPT_FACE",FACE,{"disambiguationData":[OSD([sQuery(id+"F28.wireOp",EDGE,"E11.0.6.0")])]})])],"derivedFrom":makeQuery(id+"F12.opExtrude","CAP_FACE",FACE,{"disambiguationData":[OSD([subQ5,subQ4,subQ3,subQ2])],"isStart":false})})],"blendedInto":[makeQuery(id+"F29.boolean.opBoolean","SPLIT",FACE,{"disambiguationData":[TD([subQ7,makeQuery(id+"F25.opChamfer","BLEND_FACE",FACE,{"disambiguationData":[OSD([subQ3])]}),subQ6,subQ1,makeQuery(id+"F29.opExtrude","SWEPT_FACE",FACE,{"disambiguationData":[OSD([sQuery(id+"F28.wireOp",EDGE,"E11.0.6.0")])]})])],"derivedFrom":makeQuery(id+"F12.opExtrude","CAP_FACE",FACE,{"disambiguationData":[OSD([subQ5,subQ4,subQ3,subQ2])],"isStart":false})})]});}
            var Q37;
            {var subQ0=sQuery(id+"F11.wireOp",EDGE,"E1.bottom");var subQ1=makeQuery(id+"F25.opChamfer","BLEND_FACE",FACE,{"disambiguationData":[OSD([subQ0])]});var subQ2=sQuery(id+"F11.wireOp",EDGE,"E1.right");var subQ3=sQuery(id+"F11.wireOp",EDGE,"E1.left");var subQ4=sQuery(id+"F11.wireOp",EDGE,"E1.top");var subQ5=makeQuery(id+"F27.opChamfer","BLEND_FACE",FACE,{"disambiguationData":[OSD([subQ0,subQ4,subQ3,subQ2,sQuery(id+"F22.wireOp",EDGE,"E9")])]});var subQ6=sQuery(id+"F28.wireOp",EDGE,"E11.0.4.0");var subQ7=makeQuery(id+"F29.opExtrude","SWEPT_FACE",FACE,{"disambiguationData":[OSD([subQ6])]});Q37=makeQuery(id+"F30.opFillet","BLEND_EDGE",EDGE,{"blendedFrom":[makeQuery(id+"F29.boolean.opBoolean","COPY",EDGE,{"disambiguationData":[TD([subQ1])],"derivedFrom":makeQuery(id+"F29.opExtrude","CAP_EDGE",EDGE,{"disambiguationData":[OSD([subQ6])],"isStart":false})}),makeQuery(id+"F29.boolean.opBoolean","SPLIT",FACE,{"disambiguationData":[TD([subQ1,subQ5,makeQuery(id+"F29.opExtrude","SWEPT_FACE",FACE,{"disambiguationData":[OSD([sQuery(id+"F28.wireOp",EDGE,"E11.0.3.1")])]}),subQ7])],"derivedFrom":makeQuery(id+"F12.opExtrude","CAP_FACE",FACE,{"disambiguationData":[OSD([subQ0,subQ4,subQ3,subQ2])],"isStart":false})})],"blendedInto":[makeQuery(id+"F29.boolean.opBoolean","SPLIT",FACE,{"disambiguationData":[TD([subQ1,subQ5,makeQuery(id+"F29.opExtrude","SWEPT_FACE",FACE,{"disambiguationData":[OSD([sQuery(id+"F28.wireOp",EDGE,"E11.0.3.1")])]}),subQ7])],"derivedFrom":makeQuery(id+"F12.opExtrude","CAP_FACE",FACE,{"disambiguationData":[OSD([subQ0,subQ4,subQ3,subQ2])],"isStart":false})})]});}
            var Q38;
            {var subQ0=sQuery(id+"F11.wireOp",EDGE,"E1.bottom");var subQ1=makeQuery(id+"F25.opChamfer","BLEND_FACE",FACE,{"disambiguationData":[OSD([subQ0])]});var subQ2=sQuery(id+"F28.wireOp",EDGE,"E11.0.4.1");var subQ3=makeQuery(id+"F29.opExtrude","SWEPT_FACE",FACE,{"disambiguationData":[OSD([subQ2])]});var subQ4=sQuery(id+"F11.wireOp",EDGE,"E1.right");var subQ5=sQuery(id+"F11.wireOp",EDGE,"E1.left");var subQ6=sQuery(id+"F11.wireOp",EDGE,"E1.top");var subQ7=makeQuery(id+"F27.opChamfer","BLEND_FACE",FACE,{"disambiguationData":[OSD([subQ0,subQ6,subQ5,subQ4,sQuery(id+"F22.wireOp",EDGE,"E9")])]});Q38=makeQuery(id+"F30.opFillet","BLEND_EDGE",EDGE,{"blendedFrom":[makeQuery(id+"F29.boolean.opBoolean","COPY",EDGE,{"disambiguationData":[TD([subQ1])],"derivedFrom":makeQuery(id+"F29.opExtrude","CAP_EDGE",EDGE,{"disambiguationData":[OSD([subQ2])],"isStart":false})}),makeQuery(id+"F29.boolean.opBoolean","SPLIT",FACE,{"disambiguationData":[TD([subQ1,subQ7,subQ3,makeQuery(id+"F29.opExtrude","SWEPT_FACE",FACE,{"disambiguationData":[OSD([sQuery(id+"F28.wireOp",EDGE,"E11.0.5.0")])]})])],"derivedFrom":makeQuery(id+"F12.opExtrude","CAP_FACE",FACE,{"disambiguationData":[OSD([subQ0,subQ6,subQ5,subQ4])],"isStart":false})})],"blendedInto":[makeQuery(id+"F29.boolean.opBoolean","SPLIT",FACE,{"disambiguationData":[TD([subQ1,subQ7,subQ3,makeQuery(id+"F29.opExtrude","SWEPT_FACE",FACE,{"disambiguationData":[OSD([sQuery(id+"F28.wireOp",EDGE,"E11.0.5.0")])]})])],"derivedFrom":makeQuery(id+"F12.opExtrude","CAP_FACE",FACE,{"disambiguationData":[OSD([subQ0,subQ6,subQ5,subQ4])],"isStart":false})})]});}
            var Q39;
            {var subQ0=sQuery(id+"F11.wireOp",EDGE,"E1.bottom");var subQ1=makeQuery(id+"F25.opChamfer","BLEND_FACE",FACE,{"disambiguationData":[OSD([subQ0])]});var subQ2=sQuery(id+"F11.wireOp",EDGE,"E1.right");var subQ3=sQuery(id+"F11.wireOp",EDGE,"E1.left");var subQ4=sQuery(id+"F11.wireOp",EDGE,"E1.top");var subQ5=makeQuery(id+"F27.opChamfer","BLEND_FACE",FACE,{"disambiguationData":[OSD([subQ0,subQ4,subQ3,subQ2,sQuery(id+"F22.wireOp",EDGE,"E9")])]});var subQ6=sQuery(id+"F28.wireOp",EDGE,"E11.0.3.1");var subQ7=makeQuery(id+"F29.opExtrude","SWEPT_FACE",FACE,{"disambiguationData":[OSD([subQ6])]});Q39=makeQuery(id+"F30.opFillet","BLEND_EDGE",EDGE,{"blendedFrom":[makeQuery(id+"F29.boolean.opBoolean","COPY",EDGE,{"disambiguationData":[TD([subQ1])],"derivedFrom":makeQuery(id+"F29.opExtrude","CAP_EDGE",EDGE,{"disambiguationData":[OSD([subQ6])],"isStart":false})}),makeQuery(id+"F29.boolean.opBoolean","SPLIT",FACE,{"disambiguationData":[TD([subQ1,subQ5,subQ7,makeQuery(id+"F29.opExtrude","SWEPT_FACE",FACE,{"disambiguationData":[OSD([sQuery(id+"F28.wireOp",EDGE,"E11.0.4.0")])]})])],"derivedFrom":makeQuery(id+"F12.opExtrude","CAP_FACE",FACE,{"disambiguationData":[OSD([subQ0,subQ4,subQ3,subQ2])],"isStart":false})})],"blendedInto":[makeQuery(id+"F29.boolean.opBoolean","SPLIT",FACE,{"disambiguationData":[TD([subQ1,subQ5,subQ7,makeQuery(id+"F29.opExtrude","SWEPT_FACE",FACE,{"disambiguationData":[OSD([sQuery(id+"F28.wireOp",EDGE,"E11.0.4.0")])]})])],"derivedFrom":makeQuery(id+"F12.opExtrude","CAP_FACE",FACE,{"disambiguationData":[OSD([subQ0,subQ4,subQ3,subQ2])],"isStart":false})})]});}
            fillet(context, id + "F31", {"entities" : qUnion([Q0, Q1, Q2, Q3, Q4, Q5, Q6, Q7, Q8, Q9, Q10, Q11, Q12, Q13, Q14, Q15, Q16, Q17, Q18, Q19, Q20, Q21, Q22, Q23, Q24, Q25, Q26, Q27, Q28, Q29, Q30, Q31, Q32, Q33, Q34, Q35, Q36, Q37, Q38, Q39]), "radius" : 25 * mm, "tangentPropagation" : true, "allowEdgeOverflow" : false});
        }
    });
